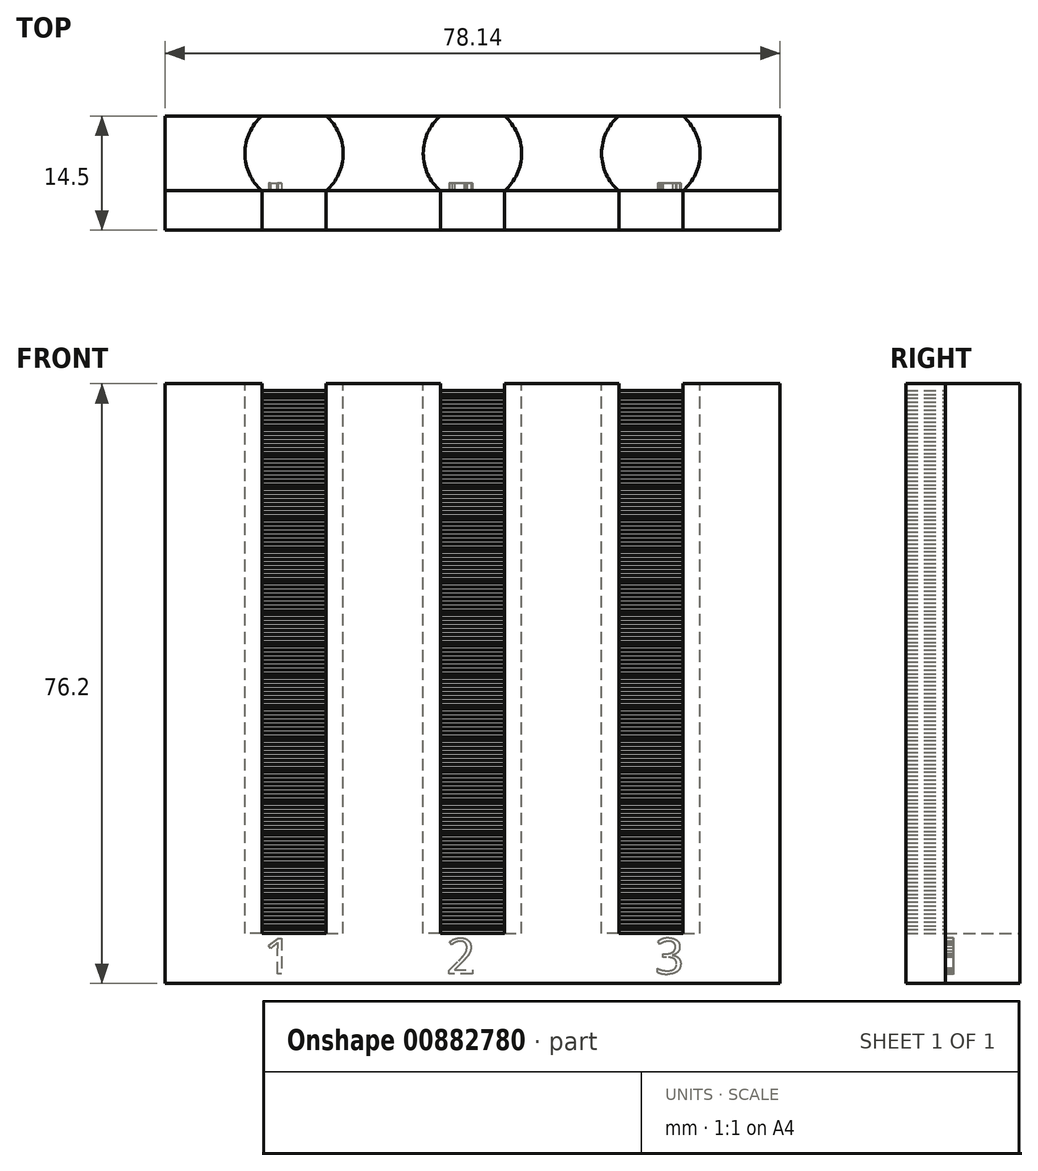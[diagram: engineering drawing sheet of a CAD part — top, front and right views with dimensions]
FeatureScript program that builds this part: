
annotation { "Feature Type Name" : "Feature", "Feature Type Description" : "" }
export const myFeature = defineFeature(function(context is Context, id is Id, definition is map)
    precondition{}
    {
        {
            var Q0;
            Q0=qCreatedBy(makeId("Top.planeOp"),FACE);
            var sketch = newSketch(context, id + "F0", { "sketchPlane" : qUnion([Q0])});
            skLineSegment(sketch, "E0.bottom", {"start": v(39.07, -4.75) * mm, "end": v(-39.07, -4.75) * mm});
            skLineSegment(sketch, "E0.top", {"start": v(39.07, 4.75) * mm, "end": v(-39.07, 4.75) * mm});
            skLineSegment(sketch, "E0.left", {"start": v(39.07, -4.75) * mm, "end": v(39.07, 4.75) * mm});
            skLineSegment(sketch, "E0.right", {"start": v(-39.07, -4.75) * mm, "end": v(-39.07, 4.75) * mm});
            skPoint(sketch, "E0.middle", {"position": v(0, 0) * mm});
            skSolve(sketch);
        }
        {
            var Q0;
            Q0 = qSketchRegion(id + "F0", true);
            extrude(context, id + "F1", {"entities" : qUnion([Q0]), "depth" : 76.2 * mm, "offsetDistance" : 25.4 * mm});
        }
        {
            var Q0;
            Q0=makeQuery(id+"F1.opExtrude","CAP_FACE",FACE,{"disambiguationData":[OSD([sQuery(id+"F0.wireOp",EDGE,"E0.bottom"),sQuery(id+"F0.wireOp",EDGE,"E0.top"),sQuery(id+"F0.wireOp",EDGE,"E0.left"),sQuery(id+"F0.wireOp",EDGE,"E0.right")])],"isStart":false});
            var sketch = newSketch(context, id + "F2", { "sketchPlane" : qUnion([Q0])});
            skCircle(sketch, "E1", {"center": v(-22.66, 0) * mm, "radius": 6.25 * mm});
            skCircle(sketch, "E2", {"center": v(0, 0) * mm, "radius": 6.25 * mm});
            skCircle(sketch, "E3", {"center": v(22.66, 0) * mm, "radius": 6.25 * mm});
            skLineSegment(sketch, "E4", {"start": v(0, -4.75) * mm, "end": v(0, 4.75) * mm});
            skSolve(sketch);
        }
        {
            var Q0;
            Q0 = qSketchRegion(id + "F2", true);
            extrude(context, id + "F3", {"entities" : qUnion([Q0]), "operationType" : NewBodyOperationType.REMOVE, "oppositeDirection" : true, "depth" : 69.85 * mm, "offsetDistance" : 25.4 * mm});
        }
        {
            var Q0;
            Q0=makeQuery(id+"F1.opExtrude","SWEPT_FACE",FACE,{"disambiguationData":[OSD([sQuery(id+"F0.wireOp",EDGE,"E0.bottom")])]});
            var sketch = newSketch(context, id + "F4", { "sketchPlane" : qUnion([Q0])});
            skText(sketch, "E5", { "text": "1            2              3", "fontName": "OpenSans-Regular.ttf"});
            const initialGuessF4  = {"E5": [-0.02647, 0.00124, 1, 0, 0.00453]};
            skSetInitialGuess(sketch, initialGuessF4);
            skSolve(sketch);
        }
        {
            var Q0;
            Q0 = qSketchRegion(id + "F4", true);
            extrude(context, id + "F5", {"entities" : qUnion([Q0]), "operationType" : NewBodyOperationType.REMOVE, "oppositeDirection" : true, "depth" : 1 * mm, "offsetDistance" : 25.4 * mm});
        }
        {
            var Q0;
            Q0=makeQuery(id+"F1.opExtrude","SWEPT_FACE",FACE,{"disambiguationData":[OSD([sQuery(id+"F0.wireOp",EDGE,"E0.bottom")])]});
            var sketch = newSketch(context, id + "F6", { "sketchPlane" : qUnion([Q0])});
            skLineSegment(sketch, "E6.bottom", {"start": v(-18.6, 6.85) * mm, "end": v(-26.72, 6.85) * mm});
            skLineSegment(sketch, "E6.top", {"start": v(-18.6, 7.35) * mm, "end": v(-26.72, 7.35) * mm});
            skLineSegment(sketch, "E6.left", {"start": v(-18.6, 6.85) * mm, "end": v(-18.6, 7.35) * mm});
            skLineSegment(sketch, "E6.right", {"start": v(-26.72, 6.85) * mm, "end": v(-26.72, 7.35) * mm});
            skLineSegment(sketch, "E7.0.1.0", {"start": v(-18.6, 8.35) * mm, "end": v(-26.72, 8.35) * mm});
            skLineSegment(sketch, "E7.0.1.1", {"start": v(-18.6, 7.85) * mm, "end": v(-26.72, 7.85) * mm});
            skLineSegment(sketch, "E7.0.1.2", {"start": v(-18.6, 7.85) * mm, "end": v(-18.6, 8.35) * mm});
            skLineSegment(sketch, "E7.0.1.3", {"start": v(-26.72, 7.85) * mm, "end": v(-26.72, 8.35) * mm});
            skLineSegment(sketch, "E7.0.2.0", {"start": v(-18.6, 9.35) * mm, "end": v(-26.72, 9.35) * mm});
            skLineSegment(sketch, "E7.0.2.1", {"start": v(-18.6, 8.85) * mm, "end": v(-26.72, 8.85) * mm});
            skLineSegment(sketch, "E7.0.2.2", {"start": v(-18.6, 8.85) * mm, "end": v(-18.6, 9.35) * mm});
            skLineSegment(sketch, "E7.0.2.3", {"start": v(-26.72, 8.85) * mm, "end": v(-26.72, 9.35) * mm});
            skLineSegment(sketch, "E7.0.3.0", {"start": v(-18.6, 10.35) * mm, "end": v(-26.72, 10.35) * mm});
            skLineSegment(sketch, "E7.0.3.1", {"start": v(-18.6, 9.85) * mm, "end": v(-26.72, 9.85) * mm});
            skLineSegment(sketch, "E7.0.3.2", {"start": v(-18.6, 9.85) * mm, "end": v(-18.6, 10.35) * mm});
            skLineSegment(sketch, "E7.0.3.3", {"start": v(-26.72, 9.85) * mm, "end": v(-26.72, 10.35) * mm});
            skLineSegment(sketch, "E7.0.4.0", {"start": v(-18.6, 11.35) * mm, "end": v(-26.72, 11.35) * mm});
            skLineSegment(sketch, "E7.0.4.1", {"start": v(-18.6, 10.85) * mm, "end": v(-26.72, 10.85) * mm});
            skLineSegment(sketch, "E7.0.4.2", {"start": v(-18.6, 10.85) * mm, "end": v(-18.6, 11.35) * mm});
            skLineSegment(sketch, "E7.0.4.3", {"start": v(-26.72, 10.85) * mm, "end": v(-26.72, 11.35) * mm});
            skLineSegment(sketch, "E7.0.5.0", {"start": v(-18.6, 12.35) * mm, "end": v(-26.72, 12.35) * mm});
            skLineSegment(sketch, "E7.0.5.1", {"start": v(-18.6, 11.85) * mm, "end": v(-26.72, 11.85) * mm});
            skLineSegment(sketch, "E7.0.5.2", {"start": v(-18.6, 11.85) * mm, "end": v(-18.6, 12.35) * mm});
            skLineSegment(sketch, "E7.0.5.3", {"start": v(-26.72, 11.85) * mm, "end": v(-26.72, 12.35) * mm});
            skLineSegment(sketch, "E7.0.6.0", {"start": v(-18.6, 13.35) * mm, "end": v(-26.72, 13.35) * mm});
            skLineSegment(sketch, "E7.0.6.1", {"start": v(-18.6, 12.85) * mm, "end": v(-26.72, 12.85) * mm});
            skLineSegment(sketch, "E7.0.6.2", {"start": v(-18.6, 12.85) * mm, "end": v(-18.6, 13.35) * mm});
            skLineSegment(sketch, "E7.0.6.3", {"start": v(-26.72, 12.85) * mm, "end": v(-26.72, 13.35) * mm});
            skLineSegment(sketch, "E7.0.7.0", {"start": v(-18.6, 14.35) * mm, "end": v(-26.72, 14.35) * mm});
            skLineSegment(sketch, "E7.0.7.1", {"start": v(-18.6, 13.85) * mm, "end": v(-26.72, 13.85) * mm});
            skLineSegment(sketch, "E7.0.7.2", {"start": v(-18.6, 13.85) * mm, "end": v(-18.6, 14.35) * mm});
            skLineSegment(sketch, "E7.0.7.3", {"start": v(-26.72, 13.85) * mm, "end": v(-26.72, 14.35) * mm});
            skLineSegment(sketch, "E7.0.8.0", {"start": v(-18.6, 15.35) * mm, "end": v(-26.72, 15.35) * mm});
            skLineSegment(sketch, "E7.0.8.1", {"start": v(-18.6, 14.85) * mm, "end": v(-26.72, 14.85) * mm});
            skLineSegment(sketch, "E7.0.8.2", {"start": v(-18.6, 14.85) * mm, "end": v(-18.6, 15.35) * mm});
            skLineSegment(sketch, "E7.0.8.3", {"start": v(-26.72, 14.85) * mm, "end": v(-26.72, 15.35) * mm});
            skLineSegment(sketch, "E7.0.9.0", {"start": v(-18.6, 16.35) * mm, "end": v(-26.72, 16.35) * mm});
            skLineSegment(sketch, "E7.0.9.1", {"start": v(-18.6, 15.85) * mm, "end": v(-26.72, 15.85) * mm});
            skLineSegment(sketch, "E7.0.9.2", {"start": v(-18.6, 15.85) * mm, "end": v(-18.6, 16.35) * mm});
            skLineSegment(sketch, "E7.0.9.3", {"start": v(-26.72, 15.85) * mm, "end": v(-26.72, 16.35) * mm});
            skLineSegment(sketch, "E7.0.10.0", {"start": v(-18.6, 17.35) * mm, "end": v(-26.72, 17.35) * mm});
            skLineSegment(sketch, "E7.0.10.1", {"start": v(-18.6, 16.85) * mm, "end": v(-26.72, 16.85) * mm});
            skLineSegment(sketch, "E7.0.10.2", {"start": v(-18.6, 16.85) * mm, "end": v(-18.6, 17.35) * mm});
            skLineSegment(sketch, "E7.0.10.3", {"start": v(-26.72, 16.85) * mm, "end": v(-26.72, 17.35) * mm});
            skLineSegment(sketch, "E7.0.11.0", {"start": v(-18.6, 18.35) * mm, "end": v(-26.72, 18.35) * mm});
            skLineSegment(sketch, "E7.0.11.1", {"start": v(-18.6, 17.85) * mm, "end": v(-26.72, 17.85) * mm});
            skLineSegment(sketch, "E7.0.11.2", {"start": v(-18.6, 17.85) * mm, "end": v(-18.6, 18.35) * mm});
            skLineSegment(sketch, "E7.0.11.3", {"start": v(-26.72, 17.85) * mm, "end": v(-26.72, 18.35) * mm});
            skLineSegment(sketch, "E7.0.12.0", {"start": v(-18.6, 19.35) * mm, "end": v(-26.72, 19.35) * mm});
            skLineSegment(sketch, "E7.0.12.1", {"start": v(-18.6, 18.85) * mm, "end": v(-26.72, 18.85) * mm});
            skLineSegment(sketch, "E7.0.12.2", {"start": v(-18.6, 18.85) * mm, "end": v(-18.6, 19.35) * mm});
            skLineSegment(sketch, "E7.0.12.3", {"start": v(-26.72, 18.85) * mm, "end": v(-26.72, 19.35) * mm});
            skLineSegment(sketch, "E7.0.13.0", {"start": v(-18.6, 20.35) * mm, "end": v(-26.72, 20.35) * mm});
            skLineSegment(sketch, "E7.0.13.1", {"start": v(-18.6, 19.85) * mm, "end": v(-26.72, 19.85) * mm});
            skLineSegment(sketch, "E7.0.13.2", {"start": v(-18.6, 19.85) * mm, "end": v(-18.6, 20.35) * mm});
            skLineSegment(sketch, "E7.0.13.3", {"start": v(-26.72, 19.85) * mm, "end": v(-26.72, 20.35) * mm});
            skLineSegment(sketch, "E7.0.14.0", {"start": v(-18.6, 21.35) * mm, "end": v(-26.72, 21.35) * mm});
            skLineSegment(sketch, "E7.0.14.1", {"start": v(-18.6, 20.85) * mm, "end": v(-26.72, 20.85) * mm});
            skLineSegment(sketch, "E7.0.14.2", {"start": v(-18.6, 20.85) * mm, "end": v(-18.6, 21.35) * mm});
            skLineSegment(sketch, "E7.0.14.3", {"start": v(-26.72, 20.85) * mm, "end": v(-26.72, 21.35) * mm});
            skLineSegment(sketch, "E7.0.15.0", {"start": v(-18.6, 22.35) * mm, "end": v(-26.72, 22.35) * mm});
            skLineSegment(sketch, "E7.0.15.1", {"start": v(-18.6, 21.85) * mm, "end": v(-26.72, 21.85) * mm});
            skLineSegment(sketch, "E7.0.15.2", {"start": v(-18.6, 21.85) * mm, "end": v(-18.6, 22.35) * mm});
            skLineSegment(sketch, "E7.0.15.3", {"start": v(-26.72, 21.85) * mm, "end": v(-26.72, 22.35) * mm});
            skLineSegment(sketch, "E7.0.16.0", {"start": v(-18.6, 23.35) * mm, "end": v(-26.72, 23.35) * mm});
            skLineSegment(sketch, "E7.0.16.1", {"start": v(-18.6, 22.85) * mm, "end": v(-26.72, 22.85) * mm});
            skLineSegment(sketch, "E7.0.16.2", {"start": v(-18.6, 22.85) * mm, "end": v(-18.6, 23.35) * mm});
            skLineSegment(sketch, "E7.0.16.3", {"start": v(-26.72, 22.85) * mm, "end": v(-26.72, 23.35) * mm});
            skLineSegment(sketch, "E7.0.17.0", {"start": v(-18.6, 24.35) * mm, "end": v(-26.72, 24.35) * mm});
            skLineSegment(sketch, "E7.0.17.1", {"start": v(-18.6, 23.85) * mm, "end": v(-26.72, 23.85) * mm});
            skLineSegment(sketch, "E7.0.17.2", {"start": v(-18.6, 23.85) * mm, "end": v(-18.6, 24.35) * mm});
            skLineSegment(sketch, "E7.0.17.3", {"start": v(-26.72, 23.85) * mm, "end": v(-26.72, 24.35) * mm});
            skLineSegment(sketch, "E7.0.18.0", {"start": v(-18.6, 25.35) * mm, "end": v(-26.72, 25.35) * mm});
            skLineSegment(sketch, "E7.0.18.1", {"start": v(-18.6, 24.85) * mm, "end": v(-26.72, 24.85) * mm});
            skLineSegment(sketch, "E7.0.18.2", {"start": v(-18.6, 24.85) * mm, "end": v(-18.6, 25.35) * mm});
            skLineSegment(sketch, "E7.0.18.3", {"start": v(-26.72, 24.85) * mm, "end": v(-26.72, 25.35) * mm});
            skLineSegment(sketch, "E7.0.19.0", {"start": v(-18.6, 26.35) * mm, "end": v(-26.72, 26.35) * mm});
            skLineSegment(sketch, "E7.0.19.1", {"start": v(-18.6, 25.85) * mm, "end": v(-26.72, 25.85) * mm});
            skLineSegment(sketch, "E7.0.19.2", {"start": v(-18.6, 25.85) * mm, "end": v(-18.6, 26.35) * mm});
            skLineSegment(sketch, "E7.0.19.3", {"start": v(-26.72, 25.85) * mm, "end": v(-26.72, 26.35) * mm});
            skLineSegment(sketch, "E7.0.20.0", {"start": v(-18.6, 27.35) * mm, "end": v(-26.72, 27.35) * mm});
            skLineSegment(sketch, "E7.0.20.1", {"start": v(-18.6, 26.85) * mm, "end": v(-26.72, 26.85) * mm});
            skLineSegment(sketch, "E7.0.20.2", {"start": v(-18.6, 26.85) * mm, "end": v(-18.6, 27.35) * mm});
            skLineSegment(sketch, "E7.0.20.3", {"start": v(-26.72, 26.85) * mm, "end": v(-26.72, 27.35) * mm});
            skLineSegment(sketch, "E7.0.21.0", {"start": v(-18.6, 28.35) * mm, "end": v(-26.72, 28.35) * mm});
            skLineSegment(sketch, "E7.0.21.1", {"start": v(-18.6, 27.85) * mm, "end": v(-26.72, 27.85) * mm});
            skLineSegment(sketch, "E7.0.21.2", {"start": v(-18.6, 27.85) * mm, "end": v(-18.6, 28.35) * mm});
            skLineSegment(sketch, "E7.0.21.3", {"start": v(-26.72, 27.85) * mm, "end": v(-26.72, 28.35) * mm});
            skLineSegment(sketch, "E7.0.22.0", {"start": v(-18.6, 29.35) * mm, "end": v(-26.72, 29.35) * mm});
            skLineSegment(sketch, "E7.0.22.1", {"start": v(-18.6, 28.85) * mm, "end": v(-26.72, 28.85) * mm});
            skLineSegment(sketch, "E7.0.22.2", {"start": v(-18.6, 28.85) * mm, "end": v(-18.6, 29.35) * mm});
            skLineSegment(sketch, "E7.0.22.3", {"start": v(-26.72, 28.85) * mm, "end": v(-26.72, 29.35) * mm});
            skLineSegment(sketch, "E7.0.23.0", {"start": v(-18.6, 30.35) * mm, "end": v(-26.72, 30.35) * mm});
            skLineSegment(sketch, "E7.0.23.1", {"start": v(-18.6, 29.85) * mm, "end": v(-26.72, 29.85) * mm});
            skLineSegment(sketch, "E7.0.23.2", {"start": v(-18.6, 29.85) * mm, "end": v(-18.6, 30.35) * mm});
            skLineSegment(sketch, "E7.0.23.3", {"start": v(-26.72, 29.85) * mm, "end": v(-26.72, 30.35) * mm});
            skLineSegment(sketch, "E7.0.24.0", {"start": v(-18.6, 31.35) * mm, "end": v(-26.72, 31.35) * mm});
            skLineSegment(sketch, "E7.0.24.1", {"start": v(-18.6, 30.85) * mm, "end": v(-26.72, 30.85) * mm});
            skLineSegment(sketch, "E7.0.24.2", {"start": v(-18.6, 30.85) * mm, "end": v(-18.6, 31.35) * mm});
            skLineSegment(sketch, "E7.0.24.3", {"start": v(-26.72, 30.85) * mm, "end": v(-26.72, 31.35) * mm});
            skLineSegment(sketch, "E7.0.25.0", {"start": v(-18.6, 32.35) * mm, "end": v(-26.72, 32.35) * mm});
            skLineSegment(sketch, "E7.0.25.1", {"start": v(-18.6, 31.85) * mm, "end": v(-26.72, 31.85) * mm});
            skLineSegment(sketch, "E7.0.25.2", {"start": v(-18.6, 31.85) * mm, "end": v(-18.6, 32.35) * mm});
            skLineSegment(sketch, "E7.0.25.3", {"start": v(-26.72, 31.85) * mm, "end": v(-26.72, 32.35) * mm});
            skLineSegment(sketch, "E7.0.26.0", {"start": v(-18.6, 33.35) * mm, "end": v(-26.72, 33.35) * mm});
            skLineSegment(sketch, "E7.0.26.1", {"start": v(-18.6, 32.85) * mm, "end": v(-26.72, 32.85) * mm});
            skLineSegment(sketch, "E7.0.26.2", {"start": v(-18.6, 32.85) * mm, "end": v(-18.6, 33.35) * mm});
            skLineSegment(sketch, "E7.0.26.3", {"start": v(-26.72, 32.85) * mm, "end": v(-26.72, 33.35) * mm});
            skLineSegment(sketch, "E7.0.27.0", {"start": v(-18.6, 34.35) * mm, "end": v(-26.72, 34.35) * mm});
            skLineSegment(sketch, "E7.0.27.1", {"start": v(-18.6, 33.85) * mm, "end": v(-26.72, 33.85) * mm});
            skLineSegment(sketch, "E7.0.27.2", {"start": v(-18.6, 33.85) * mm, "end": v(-18.6, 34.35) * mm});
            skLineSegment(sketch, "E7.0.27.3", {"start": v(-26.72, 33.85) * mm, "end": v(-26.72, 34.35) * mm});
            skLineSegment(sketch, "E7.0.28.0", {"start": v(-18.6, 35.35) * mm, "end": v(-26.72, 35.35) * mm});
            skLineSegment(sketch, "E7.0.28.1", {"start": v(-18.6, 34.85) * mm, "end": v(-26.72, 34.85) * mm});
            skLineSegment(sketch, "E7.0.28.2", {"start": v(-18.6, 34.85) * mm, "end": v(-18.6, 35.35) * mm});
            skLineSegment(sketch, "E7.0.28.3", {"start": v(-26.72, 34.85) * mm, "end": v(-26.72, 35.35) * mm});
            skLineSegment(sketch, "E7.0.29.0", {"start": v(-18.6, 36.35) * mm, "end": v(-26.72, 36.35) * mm});
            skLineSegment(sketch, "E7.0.29.1", {"start": v(-18.6, 35.85) * mm, "end": v(-26.72, 35.85) * mm});
            skLineSegment(sketch, "E7.0.29.2", {"start": v(-18.6, 35.85) * mm, "end": v(-18.6, 36.35) * mm});
            skLineSegment(sketch, "E7.0.29.3", {"start": v(-26.72, 35.85) * mm, "end": v(-26.72, 36.35) * mm});
            skLineSegment(sketch, "E7.0.30.0", {"start": v(-18.6, 37.35) * mm, "end": v(-26.72, 37.35) * mm});
            skLineSegment(sketch, "E7.0.30.1", {"start": v(-18.6, 36.85) * mm, "end": v(-26.72, 36.85) * mm});
            skLineSegment(sketch, "E7.0.30.2", {"start": v(-18.6, 36.85) * mm, "end": v(-18.6, 37.35) * mm});
            skLineSegment(sketch, "E7.0.30.3", {"start": v(-26.72, 36.85) * mm, "end": v(-26.72, 37.35) * mm});
            skLineSegment(sketch, "E7.0.31.0", {"start": v(-18.6, 38.35) * mm, "end": v(-26.72, 38.35) * mm});
            skLineSegment(sketch, "E7.0.31.1", {"start": v(-18.6, 37.85) * mm, "end": v(-26.72, 37.85) * mm});
            skLineSegment(sketch, "E7.0.31.2", {"start": v(-18.6, 37.85) * mm, "end": v(-18.6, 38.35) * mm});
            skLineSegment(sketch, "E7.0.31.3", {"start": v(-26.72, 37.85) * mm, "end": v(-26.72, 38.35) * mm});
            skLineSegment(sketch, "E7.0.32.0", {"start": v(-18.6, 39.35) * mm, "end": v(-26.72, 39.35) * mm});
            skLineSegment(sketch, "E7.0.32.1", {"start": v(-18.6, 38.85) * mm, "end": v(-26.72, 38.85) * mm});
            skLineSegment(sketch, "E7.0.32.2", {"start": v(-18.6, 38.85) * mm, "end": v(-18.6, 39.35) * mm});
            skLineSegment(sketch, "E7.0.32.3", {"start": v(-26.72, 38.85) * mm, "end": v(-26.72, 39.35) * mm});
            skLineSegment(sketch, "E7.0.33.0", {"start": v(-18.6, 40.35) * mm, "end": v(-26.72, 40.35) * mm});
            skLineSegment(sketch, "E7.0.33.1", {"start": v(-18.6, 39.85) * mm, "end": v(-26.72, 39.85) * mm});
            skLineSegment(sketch, "E7.0.33.2", {"start": v(-18.6, 39.85) * mm, "end": v(-18.6, 40.35) * mm});
            skLineSegment(sketch, "E7.0.33.3", {"start": v(-26.72, 39.85) * mm, "end": v(-26.72, 40.35) * mm});
            skLineSegment(sketch, "E7.0.34.0", {"start": v(-18.6, 41.35) * mm, "end": v(-26.72, 41.35) * mm});
            skLineSegment(sketch, "E7.0.34.1", {"start": v(-18.6, 40.85) * mm, "end": v(-26.72, 40.85) * mm});
            skLineSegment(sketch, "E7.0.34.2", {"start": v(-18.6, 40.85) * mm, "end": v(-18.6, 41.35) * mm});
            skLineSegment(sketch, "E7.0.34.3", {"start": v(-26.72, 40.85) * mm, "end": v(-26.72, 41.35) * mm});
            skLineSegment(sketch, "E7.0.35.0", {"start": v(-18.6, 42.35) * mm, "end": v(-26.72, 42.35) * mm});
            skLineSegment(sketch, "E7.0.35.1", {"start": v(-18.6, 41.85) * mm, "end": v(-26.72, 41.85) * mm});
            skLineSegment(sketch, "E7.0.35.2", {"start": v(-18.6, 41.85) * mm, "end": v(-18.6, 42.35) * mm});
            skLineSegment(sketch, "E7.0.35.3", {"start": v(-26.72, 41.85) * mm, "end": v(-26.72, 42.35) * mm});
            skLineSegment(sketch, "E7.0.36.0", {"start": v(-18.6, 43.35) * mm, "end": v(-26.72, 43.35) * mm});
            skLineSegment(sketch, "E7.0.36.1", {"start": v(-18.6, 42.85) * mm, "end": v(-26.72, 42.85) * mm});
            skLineSegment(sketch, "E7.0.36.2", {"start": v(-18.6, 42.85) * mm, "end": v(-18.6, 43.35) * mm});
            skLineSegment(sketch, "E7.0.36.3", {"start": v(-26.72, 42.85) * mm, "end": v(-26.72, 43.35) * mm});
            skLineSegment(sketch, "E7.0.37.0", {"start": v(-18.6, 44.35) * mm, "end": v(-26.72, 44.35) * mm});
            skLineSegment(sketch, "E7.0.37.1", {"start": v(-18.6, 43.85) * mm, "end": v(-26.72, 43.85) * mm});
            skLineSegment(sketch, "E7.0.37.2", {"start": v(-18.6, 43.85) * mm, "end": v(-18.6, 44.35) * mm});
            skLineSegment(sketch, "E7.0.37.3", {"start": v(-26.72, 43.85) * mm, "end": v(-26.72, 44.35) * mm});
            skLineSegment(sketch, "E7.0.38.0", {"start": v(-18.6, 45.35) * mm, "end": v(-26.72, 45.35) * mm});
            skLineSegment(sketch, "E7.0.38.1", {"start": v(-18.6, 44.85) * mm, "end": v(-26.72, 44.85) * mm});
            skLineSegment(sketch, "E7.0.38.2", {"start": v(-18.6, 44.85) * mm, "end": v(-18.6, 45.35) * mm});
            skLineSegment(sketch, "E7.0.38.3", {"start": v(-26.72, 44.85) * mm, "end": v(-26.72, 45.35) * mm});
            skLineSegment(sketch, "E7.0.39.0", {"start": v(-18.6, 46.35) * mm, "end": v(-26.72, 46.35) * mm});
            skLineSegment(sketch, "E7.0.39.1", {"start": v(-18.6, 45.85) * mm, "end": v(-26.72, 45.85) * mm});
            skLineSegment(sketch, "E7.0.39.2", {"start": v(-18.6, 45.85) * mm, "end": v(-18.6, 46.35) * mm});
            skLineSegment(sketch, "E7.0.39.3", {"start": v(-26.72, 45.85) * mm, "end": v(-26.72, 46.35) * mm});
            skLineSegment(sketch, "E7.0.40.0", {"start": v(-18.6, 47.35) * mm, "end": v(-26.72, 47.35) * mm});
            skLineSegment(sketch, "E7.0.40.1", {"start": v(-18.6, 46.85) * mm, "end": v(-26.72, 46.85) * mm});
            skLineSegment(sketch, "E7.0.40.2", {"start": v(-18.6, 46.85) * mm, "end": v(-18.6, 47.35) * mm});
            skLineSegment(sketch, "E7.0.40.3", {"start": v(-26.72, 46.85) * mm, "end": v(-26.72, 47.35) * mm});
            skLineSegment(sketch, "E7.0.41.0", {"start": v(-18.6, 48.35) * mm, "end": v(-26.72, 48.35) * mm});
            skLineSegment(sketch, "E7.0.41.1", {"start": v(-18.6, 47.85) * mm, "end": v(-26.72, 47.85) * mm});
            skLineSegment(sketch, "E7.0.41.2", {"start": v(-18.6, 47.85) * mm, "end": v(-18.6, 48.35) * mm});
            skLineSegment(sketch, "E7.0.41.3", {"start": v(-26.72, 47.85) * mm, "end": v(-26.72, 48.35) * mm});
            skLineSegment(sketch, "E7.0.42.0", {"start": v(-18.6, 49.35) * mm, "end": v(-26.72, 49.35) * mm});
            skLineSegment(sketch, "E7.0.42.1", {"start": v(-18.6, 48.85) * mm, "end": v(-26.72, 48.85) * mm});
            skLineSegment(sketch, "E7.0.42.2", {"start": v(-18.6, 48.85) * mm, "end": v(-18.6, 49.35) * mm});
            skLineSegment(sketch, "E7.0.42.3", {"start": v(-26.72, 48.85) * mm, "end": v(-26.72, 49.35) * mm});
            skLineSegment(sketch, "E7.0.43.0", {"start": v(-18.6, 50.35) * mm, "end": v(-26.72, 50.35) * mm});
            skLineSegment(sketch, "E7.0.43.1", {"start": v(-18.6, 49.85) * mm, "end": v(-26.72, 49.85) * mm});
            skLineSegment(sketch, "E7.0.43.2", {"start": v(-18.6, 49.85) * mm, "end": v(-18.6, 50.35) * mm});
            skLineSegment(sketch, "E7.0.43.3", {"start": v(-26.72, 49.85) * mm, "end": v(-26.72, 50.35) * mm});
            skLineSegment(sketch, "E7.0.44.0", {"start": v(-18.6, 51.35) * mm, "end": v(-26.72, 51.35) * mm});
            skLineSegment(sketch, "E7.0.44.1", {"start": v(-18.6, 50.85) * mm, "end": v(-26.72, 50.85) * mm});
            skLineSegment(sketch, "E7.0.44.2", {"start": v(-18.6, 50.85) * mm, "end": v(-18.6, 51.35) * mm});
            skLineSegment(sketch, "E7.0.44.3", {"start": v(-26.72, 50.85) * mm, "end": v(-26.72, 51.35) * mm});
            skLineSegment(sketch, "E7.0.45.0", {"start": v(-18.6, 52.35) * mm, "end": v(-26.72, 52.35) * mm});
            skLineSegment(sketch, "E7.0.45.1", {"start": v(-18.6, 51.85) * mm, "end": v(-26.72, 51.85) * mm});
            skLineSegment(sketch, "E7.0.45.2", {"start": v(-18.6, 51.85) * mm, "end": v(-18.6, 52.35) * mm});
            skLineSegment(sketch, "E7.0.45.3", {"start": v(-26.72, 51.85) * mm, "end": v(-26.72, 52.35) * mm});
            skLineSegment(sketch, "E7.0.46.0", {"start": v(-18.6, 53.35) * mm, "end": v(-26.72, 53.35) * mm});
            skLineSegment(sketch, "E7.0.46.1", {"start": v(-18.6, 52.85) * mm, "end": v(-26.72, 52.85) * mm});
            skLineSegment(sketch, "E7.0.46.2", {"start": v(-18.6, 52.85) * mm, "end": v(-18.6, 53.35) * mm});
            skLineSegment(sketch, "E7.0.46.3", {"start": v(-26.72, 52.85) * mm, "end": v(-26.72, 53.35) * mm});
            skLineSegment(sketch, "E7.0.47.0", {"start": v(-18.6, 54.35) * mm, "end": v(-26.72, 54.35) * mm});
            skLineSegment(sketch, "E7.0.47.1", {"start": v(-18.6, 53.85) * mm, "end": v(-26.72, 53.85) * mm});
            skLineSegment(sketch, "E7.0.47.2", {"start": v(-18.6, 53.85) * mm, "end": v(-18.6, 54.35) * mm});
            skLineSegment(sketch, "E7.0.47.3", {"start": v(-26.72, 53.85) * mm, "end": v(-26.72, 54.35) * mm});
            skLineSegment(sketch, "E7.0.48.0", {"start": v(-18.6, 55.35) * mm, "end": v(-26.72, 55.35) * mm});
            skLineSegment(sketch, "E7.0.48.1", {"start": v(-18.6, 54.85) * mm, "end": v(-26.72, 54.85) * mm});
            skLineSegment(sketch, "E7.0.48.2", {"start": v(-18.6, 54.85) * mm, "end": v(-18.6, 55.35) * mm});
            skLineSegment(sketch, "E7.0.48.3", {"start": v(-26.72, 54.85) * mm, "end": v(-26.72, 55.35) * mm});
            skLineSegment(sketch, "E7.0.49.0", {"start": v(-18.6, 56.35) * mm, "end": v(-26.72, 56.35) * mm});
            skLineSegment(sketch, "E7.0.49.1", {"start": v(-18.6, 55.85) * mm, "end": v(-26.72, 55.85) * mm});
            skLineSegment(sketch, "E7.0.49.2", {"start": v(-18.6, 55.85) * mm, "end": v(-18.6, 56.35) * mm});
            skLineSegment(sketch, "E7.0.49.3", {"start": v(-26.72, 55.85) * mm, "end": v(-26.72, 56.35) * mm});
            skLineSegment(sketch, "E7.0.50.0", {"start": v(-18.6, 57.35) * mm, "end": v(-26.72, 57.35) * mm});
            skLineSegment(sketch, "E7.0.50.1", {"start": v(-18.6, 56.85) * mm, "end": v(-26.72, 56.85) * mm});
            skLineSegment(sketch, "E7.0.50.2", {"start": v(-18.6, 56.85) * mm, "end": v(-18.6, 57.35) * mm});
            skLineSegment(sketch, "E7.0.50.3", {"start": v(-26.72, 56.85) * mm, "end": v(-26.72, 57.35) * mm});
            skLineSegment(sketch, "E7.0.51.0", {"start": v(-18.6, 58.35) * mm, "end": v(-26.72, 58.35) * mm});
            skLineSegment(sketch, "E7.0.51.1", {"start": v(-18.6, 57.85) * mm, "end": v(-26.72, 57.85) * mm});
            skLineSegment(sketch, "E7.0.51.2", {"start": v(-18.6, 57.85) * mm, "end": v(-18.6, 58.35) * mm});
            skLineSegment(sketch, "E7.0.51.3", {"start": v(-26.72, 57.85) * mm, "end": v(-26.72, 58.35) * mm});
            skLineSegment(sketch, "E7.0.52.0", {"start": v(-18.6, 59.35) * mm, "end": v(-26.72, 59.35) * mm});
            skLineSegment(sketch, "E7.0.52.1", {"start": v(-18.6, 58.85) * mm, "end": v(-26.72, 58.85) * mm});
            skLineSegment(sketch, "E7.0.52.2", {"start": v(-18.6, 58.85) * mm, "end": v(-18.6, 59.35) * mm});
            skLineSegment(sketch, "E7.0.52.3", {"start": v(-26.72, 58.85) * mm, "end": v(-26.72, 59.35) * mm});
            skLineSegment(sketch, "E7.0.53.0", {"start": v(-18.6, 60.35) * mm, "end": v(-26.72, 60.35) * mm});
            skLineSegment(sketch, "E7.0.53.1", {"start": v(-18.6, 59.85) * mm, "end": v(-26.72, 59.85) * mm});
            skLineSegment(sketch, "E7.0.53.2", {"start": v(-18.6, 59.85) * mm, "end": v(-18.6, 60.35) * mm});
            skLineSegment(sketch, "E7.0.53.3", {"start": v(-26.72, 59.85) * mm, "end": v(-26.72, 60.35) * mm});
            skLineSegment(sketch, "E7.0.54.0", {"start": v(-18.6, 61.35) * mm, "end": v(-26.72, 61.35) * mm});
            skLineSegment(sketch, "E7.0.54.1", {"start": v(-18.6, 60.85) * mm, "end": v(-26.72, 60.85) * mm});
            skLineSegment(sketch, "E7.0.54.2", {"start": v(-18.6, 60.85) * mm, "end": v(-18.6, 61.35) * mm});
            skLineSegment(sketch, "E7.0.54.3", {"start": v(-26.72, 60.85) * mm, "end": v(-26.72, 61.35) * mm});
            skLineSegment(sketch, "E7.0.55.0", {"start": v(-18.6, 62.35) * mm, "end": v(-26.72, 62.35) * mm});
            skLineSegment(sketch, "E7.0.55.1", {"start": v(-18.6, 61.85) * mm, "end": v(-26.72, 61.85) * mm});
            skLineSegment(sketch, "E7.0.55.2", {"start": v(-18.6, 61.85) * mm, "end": v(-18.6, 62.35) * mm});
            skLineSegment(sketch, "E7.0.55.3", {"start": v(-26.72, 61.85) * mm, "end": v(-26.72, 62.35) * mm});
            skLineSegment(sketch, "E7.0.56.0", {"start": v(-18.6, 63.35) * mm, "end": v(-26.72, 63.35) * mm});
            skLineSegment(sketch, "E7.0.56.1", {"start": v(-18.6, 62.85) * mm, "end": v(-26.72, 62.85) * mm});
            skLineSegment(sketch, "E7.0.56.2", {"start": v(-18.6, 62.85) * mm, "end": v(-18.6, 63.35) * mm});
            skLineSegment(sketch, "E7.0.56.3", {"start": v(-26.72, 62.85) * mm, "end": v(-26.72, 63.35) * mm});
            skLineSegment(sketch, "E7.0.57.0", {"start": v(-18.6, 64.35) * mm, "end": v(-26.72, 64.35) * mm});
            skLineSegment(sketch, "E7.0.57.1", {"start": v(-18.6, 63.85) * mm, "end": v(-26.72, 63.85) * mm});
            skLineSegment(sketch, "E7.0.57.2", {"start": v(-18.6, 63.85) * mm, "end": v(-18.6, 64.35) * mm});
            skLineSegment(sketch, "E7.0.57.3", {"start": v(-26.72, 63.85) * mm, "end": v(-26.72, 64.35) * mm});
            skLineSegment(sketch, "E7.0.58.0", {"start": v(-18.6, 65.35) * mm, "end": v(-26.72, 65.35) * mm});
            skLineSegment(sketch, "E7.0.58.1", {"start": v(-18.6, 64.85) * mm, "end": v(-26.72, 64.85) * mm});
            skLineSegment(sketch, "E7.0.58.2", {"start": v(-18.6, 64.85) * mm, "end": v(-18.6, 65.35) * mm});
            skLineSegment(sketch, "E7.0.58.3", {"start": v(-26.72, 64.85) * mm, "end": v(-26.72, 65.35) * mm});
            skLineSegment(sketch, "E7.0.59.0", {"start": v(-18.6, 66.35) * mm, "end": v(-26.72, 66.35) * mm});
            skLineSegment(sketch, "E7.0.59.1", {"start": v(-18.6, 65.85) * mm, "end": v(-26.72, 65.85) * mm});
            skLineSegment(sketch, "E7.0.59.2", {"start": v(-18.6, 65.85) * mm, "end": v(-18.6, 66.35) * mm});
            skLineSegment(sketch, "E7.0.59.3", {"start": v(-26.72, 65.85) * mm, "end": v(-26.72, 66.35) * mm});
            skLineSegment(sketch, "E7.0.60.0", {"start": v(-18.6, 67.35) * mm, "end": v(-26.72, 67.35) * mm});
            skLineSegment(sketch, "E7.0.60.1", {"start": v(-18.6, 66.85) * mm, "end": v(-26.72, 66.85) * mm});
            skLineSegment(sketch, "E7.0.60.2", {"start": v(-18.6, 66.85) * mm, "end": v(-18.6, 67.35) * mm});
            skLineSegment(sketch, "E7.0.60.3", {"start": v(-26.72, 66.85) * mm, "end": v(-26.72, 67.35) * mm});
            skLineSegment(sketch, "E7.0.61.0", {"start": v(-18.6, 68.35) * mm, "end": v(-26.72, 68.35) * mm});
            skLineSegment(sketch, "E7.0.61.1", {"start": v(-18.6, 67.85) * mm, "end": v(-26.72, 67.85) * mm});
            skLineSegment(sketch, "E7.0.61.2", {"start": v(-18.6, 67.85) * mm, "end": v(-18.6, 68.35) * mm});
            skLineSegment(sketch, "E7.0.61.3", {"start": v(-26.72, 67.85) * mm, "end": v(-26.72, 68.35) * mm});
            skLineSegment(sketch, "E7.0.62.0", {"start": v(-18.6, 69.35) * mm, "end": v(-26.72, 69.35) * mm});
            skLineSegment(sketch, "E7.0.62.1", {"start": v(-18.6, 68.85) * mm, "end": v(-26.72, 68.85) * mm});
            skLineSegment(sketch, "E7.0.62.2", {"start": v(-18.6, 68.85) * mm, "end": v(-18.6, 69.35) * mm});
            skLineSegment(sketch, "E7.0.62.3", {"start": v(-26.72, 68.85) * mm, "end": v(-26.72, 69.35) * mm});
            skLineSegment(sketch, "E7.0.63.0", {"start": v(-18.6, 70.35) * mm, "end": v(-26.72, 70.35) * mm});
            skLineSegment(sketch, "E7.0.63.1", {"start": v(-18.6, 69.85) * mm, "end": v(-26.72, 69.85) * mm});
            skLineSegment(sketch, "E7.0.63.2", {"start": v(-18.6, 69.85) * mm, "end": v(-18.6, 70.35) * mm});
            skLineSegment(sketch, "E7.0.63.3", {"start": v(-26.72, 69.85) * mm, "end": v(-26.72, 70.35) * mm});
            skLineSegment(sketch, "E7.0.64.0", {"start": v(-18.6, 71.35) * mm, "end": v(-26.72, 71.35) * mm});
            skLineSegment(sketch, "E7.0.64.1", {"start": v(-18.6, 70.85) * mm, "end": v(-26.72, 70.85) * mm});
            skLineSegment(sketch, "E7.0.64.2", {"start": v(-18.6, 70.85) * mm, "end": v(-18.6, 71.35) * mm});
            skLineSegment(sketch, "E7.0.64.3", {"start": v(-26.72, 70.85) * mm, "end": v(-26.72, 71.35) * mm});
            skLineSegment(sketch, "E7.0.65.0", {"start": v(-18.6, 72.35) * mm, "end": v(-26.72, 72.35) * mm});
            skLineSegment(sketch, "E7.0.65.1", {"start": v(-18.6, 71.85) * mm, "end": v(-26.72, 71.85) * mm});
            skLineSegment(sketch, "E7.0.65.2", {"start": v(-18.6, 71.85) * mm, "end": v(-18.6, 72.35) * mm});
            skLineSegment(sketch, "E7.0.65.3", {"start": v(-26.72, 71.85) * mm, "end": v(-26.72, 72.35) * mm});
            skLineSegment(sketch, "E7.0.66.0", {"start": v(-18.6, 73.35) * mm, "end": v(-26.72, 73.35) * mm});
            skLineSegment(sketch, "E7.0.66.1", {"start": v(-18.6, 72.85) * mm, "end": v(-26.72, 72.85) * mm});
            skLineSegment(sketch, "E7.0.66.2", {"start": v(-18.6, 72.85) * mm, "end": v(-18.6, 73.35) * mm});
            skLineSegment(sketch, "E7.0.66.3", {"start": v(-26.72, 72.85) * mm, "end": v(-26.72, 73.35) * mm});
            skLineSegment(sketch, "E7.0.67.0", {"start": v(-18.6, 74.35) * mm, "end": v(-26.72, 74.35) * mm});
            skLineSegment(sketch, "E7.0.67.1", {"start": v(-18.6, 73.85) * mm, "end": v(-26.72, 73.85) * mm});
            skLineSegment(sketch, "E7.0.67.2", {"start": v(-18.6, 73.85) * mm, "end": v(-18.6, 74.35) * mm});
            skLineSegment(sketch, "E7.0.67.3", {"start": v(-26.72, 73.85) * mm, "end": v(-26.72, 74.35) * mm});
            skLineSegment(sketch, "E7.0.68.0", {"start": v(-18.6, 75.35) * mm, "end": v(-26.72, 75.35) * mm});
            skLineSegment(sketch, "E7.0.68.1", {"start": v(-18.6, 74.85) * mm, "end": v(-26.72, 74.85) * mm});
            skLineSegment(sketch, "E7.0.68.2", {"start": v(-18.6, 74.85) * mm, "end": v(-18.6, 75.35) * mm});
            skLineSegment(sketch, "E7.0.68.3", {"start": v(-26.72, 74.85) * mm, "end": v(-26.72, 75.35) * mm});
            skLineSegment(sketch, "E7.1.0.0", {"start": v(4.06, 7.35) * mm, "end": v(-4.06, 7.35) * mm});
            skLineSegment(sketch, "E7.1.0.1", {"start": v(4.06, 6.85) * mm, "end": v(-4.06, 6.85) * mm});
            skLineSegment(sketch, "E7.1.0.2", {"start": v(4.06, 6.85) * mm, "end": v(4.06, 7.35) * mm});
            skLineSegment(sketch, "E7.1.0.3", {"start": v(-4.06, 6.85) * mm, "end": v(-4.06, 7.35) * mm});
            skLineSegment(sketch, "E7.1.1.0", {"start": v(4.06, 8.35) * mm, "end": v(-4.06, 8.35) * mm});
            skLineSegment(sketch, "E7.1.1.1", {"start": v(4.06, 7.85) * mm, "end": v(-4.06, 7.85) * mm});
            skLineSegment(sketch, "E7.1.1.2", {"start": v(4.06, 7.85) * mm, "end": v(4.06, 8.35) * mm});
            skLineSegment(sketch, "E7.1.1.3", {"start": v(-4.06, 7.85) * mm, "end": v(-4.06, 8.35) * mm});
            skLineSegment(sketch, "E7.1.2.0", {"start": v(4.06, 9.35) * mm, "end": v(-4.06, 9.35) * mm});
            skLineSegment(sketch, "E7.1.2.1", {"start": v(4.06, 8.85) * mm, "end": v(-4.06, 8.85) * mm});
            skLineSegment(sketch, "E7.1.2.2", {"start": v(4.06, 8.85) * mm, "end": v(4.06, 9.35) * mm});
            skLineSegment(sketch, "E7.1.2.3", {"start": v(-4.06, 8.85) * mm, "end": v(-4.06, 9.35) * mm});
            skLineSegment(sketch, "E7.1.3.0", {"start": v(4.06, 10.35) * mm, "end": v(-4.06, 10.35) * mm});
            skLineSegment(sketch, "E7.1.3.1", {"start": v(4.06, 9.85) * mm, "end": v(-4.06, 9.85) * mm});
            skLineSegment(sketch, "E7.1.3.2", {"start": v(4.06, 9.85) * mm, "end": v(4.06, 10.35) * mm});
            skLineSegment(sketch, "E7.1.3.3", {"start": v(-4.06, 9.85) * mm, "end": v(-4.06, 10.35) * mm});
            skLineSegment(sketch, "E7.1.4.0", {"start": v(4.06, 11.35) * mm, "end": v(-4.06, 11.35) * mm});
            skLineSegment(sketch, "E7.1.4.1", {"start": v(4.06, 10.85) * mm, "end": v(-4.06, 10.85) * mm});
            skLineSegment(sketch, "E7.1.4.2", {"start": v(4.06, 10.85) * mm, "end": v(4.06, 11.35) * mm});
            skLineSegment(sketch, "E7.1.4.3", {"start": v(-4.06, 10.85) * mm, "end": v(-4.06, 11.35) * mm});
            skLineSegment(sketch, "E7.1.5.0", {"start": v(4.06, 12.35) * mm, "end": v(-4.06, 12.35) * mm});
            skLineSegment(sketch, "E7.1.5.1", {"start": v(4.06, 11.85) * mm, "end": v(-4.06, 11.85) * mm});
            skLineSegment(sketch, "E7.1.5.2", {"start": v(4.06, 11.85) * mm, "end": v(4.06, 12.35) * mm});
            skLineSegment(sketch, "E7.1.5.3", {"start": v(-4.06, 11.85) * mm, "end": v(-4.06, 12.35) * mm});
            skLineSegment(sketch, "E7.1.6.0", {"start": v(4.06, 13.35) * mm, "end": v(-4.06, 13.35) * mm});
            skLineSegment(sketch, "E7.1.6.1", {"start": v(4.06, 12.85) * mm, "end": v(-4.06, 12.85) * mm});
            skLineSegment(sketch, "E7.1.6.2", {"start": v(4.06, 12.85) * mm, "end": v(4.06, 13.35) * mm});
            skLineSegment(sketch, "E7.1.6.3", {"start": v(-4.06, 12.85) * mm, "end": v(-4.06, 13.35) * mm});
            skLineSegment(sketch, "E7.1.7.0", {"start": v(4.06, 14.35) * mm, "end": v(-4.06, 14.35) * mm});
            skLineSegment(sketch, "E7.1.7.1", {"start": v(4.06, 13.85) * mm, "end": v(-4.06, 13.85) * mm});
            skLineSegment(sketch, "E7.1.7.2", {"start": v(4.06, 13.85) * mm, "end": v(4.06, 14.35) * mm});
            skLineSegment(sketch, "E7.1.7.3", {"start": v(-4.06, 13.85) * mm, "end": v(-4.06, 14.35) * mm});
            skLineSegment(sketch, "E7.1.8.0", {"start": v(4.06, 15.35) * mm, "end": v(-4.06, 15.35) * mm});
            skLineSegment(sketch, "E7.1.8.1", {"start": v(4.06, 14.85) * mm, "end": v(-4.06, 14.85) * mm});
            skLineSegment(sketch, "E7.1.8.2", {"start": v(4.06, 14.85) * mm, "end": v(4.06, 15.35) * mm});
            skLineSegment(sketch, "E7.1.8.3", {"start": v(-4.06, 14.85) * mm, "end": v(-4.06, 15.35) * mm});
            skLineSegment(sketch, "E7.1.9.0", {"start": v(4.06, 16.35) * mm, "end": v(-4.06, 16.35) * mm});
            skLineSegment(sketch, "E7.1.9.1", {"start": v(4.06, 15.85) * mm, "end": v(-4.06, 15.85) * mm});
            skLineSegment(sketch, "E7.1.9.2", {"start": v(4.06, 15.85) * mm, "end": v(4.06, 16.35) * mm});
            skLineSegment(sketch, "E7.1.9.3", {"start": v(-4.06, 15.85) * mm, "end": v(-4.06, 16.35) * mm});
            skLineSegment(sketch, "E7.1.10.0", {"start": v(4.06, 17.35) * mm, "end": v(-4.06, 17.35) * mm});
            skLineSegment(sketch, "E7.1.10.1", {"start": v(4.06, 16.85) * mm, "end": v(-4.06, 16.85) * mm});
            skLineSegment(sketch, "E7.1.10.2", {"start": v(4.06, 16.85) * mm, "end": v(4.06, 17.35) * mm});
            skLineSegment(sketch, "E7.1.10.3", {"start": v(-4.06, 16.85) * mm, "end": v(-4.06, 17.35) * mm});
            skLineSegment(sketch, "E7.1.11.0", {"start": v(4.06, 18.35) * mm, "end": v(-4.06, 18.35) * mm});
            skLineSegment(sketch, "E7.1.11.1", {"start": v(4.06, 17.85) * mm, "end": v(-4.06, 17.85) * mm});
            skLineSegment(sketch, "E7.1.11.2", {"start": v(4.06, 17.85) * mm, "end": v(4.06, 18.35) * mm});
            skLineSegment(sketch, "E7.1.11.3", {"start": v(-4.06, 17.85) * mm, "end": v(-4.06, 18.35) * mm});
            skLineSegment(sketch, "E7.1.12.0", {"start": v(4.06, 19.35) * mm, "end": v(-4.06, 19.35) * mm});
            skLineSegment(sketch, "E7.1.12.1", {"start": v(4.06, 18.85) * mm, "end": v(-4.06, 18.85) * mm});
            skLineSegment(sketch, "E7.1.12.2", {"start": v(4.06, 18.85) * mm, "end": v(4.06, 19.35) * mm});
            skLineSegment(sketch, "E7.1.12.3", {"start": v(-4.06, 18.85) * mm, "end": v(-4.06, 19.35) * mm});
            skLineSegment(sketch, "E7.1.13.0", {"start": v(4.06, 20.35) * mm, "end": v(-4.06, 20.35) * mm});
            skLineSegment(sketch, "E7.1.13.1", {"start": v(4.06, 19.85) * mm, "end": v(-4.06, 19.85) * mm});
            skLineSegment(sketch, "E7.1.13.2", {"start": v(4.06, 19.85) * mm, "end": v(4.06, 20.35) * mm});
            skLineSegment(sketch, "E7.1.13.3", {"start": v(-4.06, 19.85) * mm, "end": v(-4.06, 20.35) * mm});
            skLineSegment(sketch, "E7.1.14.0", {"start": v(4.06, 21.35) * mm, "end": v(-4.06, 21.35) * mm});
            skLineSegment(sketch, "E7.1.14.1", {"start": v(4.06, 20.85) * mm, "end": v(-4.06, 20.85) * mm});
            skLineSegment(sketch, "E7.1.14.2", {"start": v(4.06, 20.85) * mm, "end": v(4.06, 21.35) * mm});
            skLineSegment(sketch, "E7.1.14.3", {"start": v(-4.06, 20.85) * mm, "end": v(-4.06, 21.35) * mm});
            skLineSegment(sketch, "E7.1.15.0", {"start": v(4.06, 22.35) * mm, "end": v(-4.06, 22.35) * mm});
            skLineSegment(sketch, "E7.1.15.1", {"start": v(4.06, 21.85) * mm, "end": v(-4.06, 21.85) * mm});
            skLineSegment(sketch, "E7.1.15.2", {"start": v(4.06, 21.85) * mm, "end": v(4.06, 22.35) * mm});
            skLineSegment(sketch, "E7.1.15.3", {"start": v(-4.06, 21.85) * mm, "end": v(-4.06, 22.35) * mm});
            skLineSegment(sketch, "E7.1.16.0", {"start": v(4.06, 23.35) * mm, "end": v(-4.06, 23.35) * mm});
            skLineSegment(sketch, "E7.1.16.1", {"start": v(4.06, 22.85) * mm, "end": v(-4.06, 22.85) * mm});
            skLineSegment(sketch, "E7.1.16.2", {"start": v(4.06, 22.85) * mm, "end": v(4.06, 23.35) * mm});
            skLineSegment(sketch, "E7.1.16.3", {"start": v(-4.06, 22.85) * mm, "end": v(-4.06, 23.35) * mm});
            skLineSegment(sketch, "E7.1.17.0", {"start": v(4.06, 24.35) * mm, "end": v(-4.06, 24.35) * mm});
            skLineSegment(sketch, "E7.1.17.1", {"start": v(4.06, 23.85) * mm, "end": v(-4.06, 23.85) * mm});
            skLineSegment(sketch, "E7.1.17.2", {"start": v(4.06, 23.85) * mm, "end": v(4.06, 24.35) * mm});
            skLineSegment(sketch, "E7.1.17.3", {"start": v(-4.06, 23.85) * mm, "end": v(-4.06, 24.35) * mm});
            skLineSegment(sketch, "E7.1.18.0", {"start": v(4.06, 25.35) * mm, "end": v(-4.06, 25.35) * mm});
            skLineSegment(sketch, "E7.1.18.1", {"start": v(4.06, 24.85) * mm, "end": v(-4.06, 24.85) * mm});
            skLineSegment(sketch, "E7.1.18.2", {"start": v(4.06, 24.85) * mm, "end": v(4.06, 25.35) * mm});
            skLineSegment(sketch, "E7.1.18.3", {"start": v(-4.06, 24.85) * mm, "end": v(-4.06, 25.35) * mm});
            skLineSegment(sketch, "E7.1.19.0", {"start": v(4.06, 26.35) * mm, "end": v(-4.06, 26.35) * mm});
            skLineSegment(sketch, "E7.1.19.1", {"start": v(4.06, 25.85) * mm, "end": v(-4.06, 25.85) * mm});
            skLineSegment(sketch, "E7.1.19.2", {"start": v(4.06, 25.85) * mm, "end": v(4.06, 26.35) * mm});
            skLineSegment(sketch, "E7.1.19.3", {"start": v(-4.06, 25.85) * mm, "end": v(-4.06, 26.35) * mm});
            skLineSegment(sketch, "E7.1.20.0", {"start": v(4.06, 27.35) * mm, "end": v(-4.06, 27.35) * mm});
            skLineSegment(sketch, "E7.1.20.1", {"start": v(4.06, 26.85) * mm, "end": v(-4.06, 26.85) * mm});
            skLineSegment(sketch, "E7.1.20.2", {"start": v(4.06, 26.85) * mm, "end": v(4.06, 27.35) * mm});
            skLineSegment(sketch, "E7.1.20.3", {"start": v(-4.06, 26.85) * mm, "end": v(-4.06, 27.35) * mm});
            skLineSegment(sketch, "E7.1.21.0", {"start": v(4.06, 28.35) * mm, "end": v(-4.06, 28.35) * mm});
            skLineSegment(sketch, "E7.1.21.1", {"start": v(4.06, 27.85) * mm, "end": v(-4.06, 27.85) * mm});
            skLineSegment(sketch, "E7.1.21.2", {"start": v(4.06, 27.85) * mm, "end": v(4.06, 28.35) * mm});
            skLineSegment(sketch, "E7.1.21.3", {"start": v(-4.06, 27.85) * mm, "end": v(-4.06, 28.35) * mm});
            skLineSegment(sketch, "E7.1.22.0", {"start": v(4.06, 29.35) * mm, "end": v(-4.06, 29.35) * mm});
            skLineSegment(sketch, "E7.1.22.1", {"start": v(4.06, 28.85) * mm, "end": v(-4.06, 28.85) * mm});
            skLineSegment(sketch, "E7.1.22.2", {"start": v(4.06, 28.85) * mm, "end": v(4.06, 29.35) * mm});
            skLineSegment(sketch, "E7.1.22.3", {"start": v(-4.06, 28.85) * mm, "end": v(-4.06, 29.35) * mm});
            skLineSegment(sketch, "E7.1.23.0", {"start": v(4.06, 30.35) * mm, "end": v(-4.06, 30.35) * mm});
            skLineSegment(sketch, "E7.1.23.1", {"start": v(4.06, 29.85) * mm, "end": v(-4.06, 29.85) * mm});
            skLineSegment(sketch, "E7.1.23.2", {"start": v(4.06, 29.85) * mm, "end": v(4.06, 30.35) * mm});
            skLineSegment(sketch, "E7.1.23.3", {"start": v(-4.06, 29.85) * mm, "end": v(-4.06, 30.35) * mm});
            skLineSegment(sketch, "E7.1.24.0", {"start": v(4.06, 31.35) * mm, "end": v(-4.06, 31.35) * mm});
            skLineSegment(sketch, "E7.1.24.1", {"start": v(4.06, 30.85) * mm, "end": v(-4.06, 30.85) * mm});
            skLineSegment(sketch, "E7.1.24.2", {"start": v(4.06, 30.85) * mm, "end": v(4.06, 31.35) * mm});
            skLineSegment(sketch, "E7.1.24.3", {"start": v(-4.06, 30.85) * mm, "end": v(-4.06, 31.35) * mm});
            skLineSegment(sketch, "E7.1.25.0", {"start": v(4.06, 32.35) * mm, "end": v(-4.06, 32.35) * mm});
            skLineSegment(sketch, "E7.1.25.1", {"start": v(4.06, 31.85) * mm, "end": v(-4.06, 31.85) * mm});
            skLineSegment(sketch, "E7.1.25.2", {"start": v(4.06, 31.85) * mm, "end": v(4.06, 32.35) * mm});
            skLineSegment(sketch, "E7.1.25.3", {"start": v(-4.06, 31.85) * mm, "end": v(-4.06, 32.35) * mm});
            skLineSegment(sketch, "E7.1.26.0", {"start": v(4.06, 33.35) * mm, "end": v(-4.06, 33.35) * mm});
            skLineSegment(sketch, "E7.1.26.1", {"start": v(4.06, 32.85) * mm, "end": v(-4.06, 32.85) * mm});
            skLineSegment(sketch, "E7.1.26.2", {"start": v(4.06, 32.85) * mm, "end": v(4.06, 33.35) * mm});
            skLineSegment(sketch, "E7.1.26.3", {"start": v(-4.06, 32.85) * mm, "end": v(-4.06, 33.35) * mm});
            skLineSegment(sketch, "E7.1.27.0", {"start": v(4.06, 34.35) * mm, "end": v(-4.06, 34.35) * mm});
            skLineSegment(sketch, "E7.1.27.1", {"start": v(4.06, 33.85) * mm, "end": v(-4.06, 33.85) * mm});
            skLineSegment(sketch, "E7.1.27.2", {"start": v(4.06, 33.85) * mm, "end": v(4.06, 34.35) * mm});
            skLineSegment(sketch, "E7.1.27.3", {"start": v(-4.06, 33.85) * mm, "end": v(-4.06, 34.35) * mm});
            skLineSegment(sketch, "E7.1.28.0", {"start": v(4.06, 35.35) * mm, "end": v(-4.06, 35.35) * mm});
            skLineSegment(sketch, "E7.1.28.1", {"start": v(4.06, 34.85) * mm, "end": v(-4.06, 34.85) * mm});
            skLineSegment(sketch, "E7.1.28.2", {"start": v(4.06, 34.85) * mm, "end": v(4.06, 35.35) * mm});
            skLineSegment(sketch, "E7.1.28.3", {"start": v(-4.06, 34.85) * mm, "end": v(-4.06, 35.35) * mm});
            skLineSegment(sketch, "E7.1.29.0", {"start": v(4.06, 36.35) * mm, "end": v(-4.06, 36.35) * mm});
            skLineSegment(sketch, "E7.1.29.1", {"start": v(4.06, 35.85) * mm, "end": v(-4.06, 35.85) * mm});
            skLineSegment(sketch, "E7.1.29.2", {"start": v(4.06, 35.85) * mm, "end": v(4.06, 36.35) * mm});
            skLineSegment(sketch, "E7.1.29.3", {"start": v(-4.06, 35.85) * mm, "end": v(-4.06, 36.35) * mm});
            skLineSegment(sketch, "E7.1.30.0", {"start": v(4.06, 37.35) * mm, "end": v(-4.06, 37.35) * mm});
            skLineSegment(sketch, "E7.1.30.1", {"start": v(4.06, 36.85) * mm, "end": v(-4.06, 36.85) * mm});
            skLineSegment(sketch, "E7.1.30.2", {"start": v(4.06, 36.85) * mm, "end": v(4.06, 37.35) * mm});
            skLineSegment(sketch, "E7.1.30.3", {"start": v(-4.06, 36.85) * mm, "end": v(-4.06, 37.35) * mm});
            skLineSegment(sketch, "E7.1.31.0", {"start": v(4.06, 38.35) * mm, "end": v(-4.06, 38.35) * mm});
            skLineSegment(sketch, "E7.1.31.1", {"start": v(4.06, 37.85) * mm, "end": v(-4.06, 37.85) * mm});
            skLineSegment(sketch, "E7.1.31.2", {"start": v(4.06, 37.85) * mm, "end": v(4.06, 38.35) * mm});
            skLineSegment(sketch, "E7.1.31.3", {"start": v(-4.06, 37.85) * mm, "end": v(-4.06, 38.35) * mm});
            skLineSegment(sketch, "E7.1.32.0", {"start": v(4.06, 39.35) * mm, "end": v(-4.06, 39.35) * mm});
            skLineSegment(sketch, "E7.1.32.1", {"start": v(4.06, 38.85) * mm, "end": v(-4.06, 38.85) * mm});
            skLineSegment(sketch, "E7.1.32.2", {"start": v(4.06, 38.85) * mm, "end": v(4.06, 39.35) * mm});
            skLineSegment(sketch, "E7.1.32.3", {"start": v(-4.06, 38.85) * mm, "end": v(-4.06, 39.35) * mm});
            skLineSegment(sketch, "E7.1.33.0", {"start": v(4.06, 40.35) * mm, "end": v(-4.06, 40.35) * mm});
            skLineSegment(sketch, "E7.1.33.1", {"start": v(4.06, 39.85) * mm, "end": v(-4.06, 39.85) * mm});
            skLineSegment(sketch, "E7.1.33.2", {"start": v(4.06, 39.85) * mm, "end": v(4.06, 40.35) * mm});
            skLineSegment(sketch, "E7.1.33.3", {"start": v(-4.06, 39.85) * mm, "end": v(-4.06, 40.35) * mm});
            skLineSegment(sketch, "E7.1.34.0", {"start": v(4.06, 41.35) * mm, "end": v(-4.06, 41.35) * mm});
            skLineSegment(sketch, "E7.1.34.1", {"start": v(4.06, 40.85) * mm, "end": v(-4.06, 40.85) * mm});
            skLineSegment(sketch, "E7.1.34.2", {"start": v(4.06, 40.85) * mm, "end": v(4.06, 41.35) * mm});
            skLineSegment(sketch, "E7.1.34.3", {"start": v(-4.06, 40.85) * mm, "end": v(-4.06, 41.35) * mm});
            skLineSegment(sketch, "E7.1.35.0", {"start": v(4.06, 42.35) * mm, "end": v(-4.06, 42.35) * mm});
            skLineSegment(sketch, "E7.1.35.1", {"start": v(4.06, 41.85) * mm, "end": v(-4.06, 41.85) * mm});
            skLineSegment(sketch, "E7.1.35.2", {"start": v(4.06, 41.85) * mm, "end": v(4.06, 42.35) * mm});
            skLineSegment(sketch, "E7.1.35.3", {"start": v(-4.06, 41.85) * mm, "end": v(-4.06, 42.35) * mm});
            skLineSegment(sketch, "E7.1.36.0", {"start": v(4.06, 43.35) * mm, "end": v(-4.06, 43.35) * mm});
            skLineSegment(sketch, "E7.1.36.1", {"start": v(4.06, 42.85) * mm, "end": v(-4.06, 42.85) * mm});
            skLineSegment(sketch, "E7.1.36.2", {"start": v(4.06, 42.85) * mm, "end": v(4.06, 43.35) * mm});
            skLineSegment(sketch, "E7.1.36.3", {"start": v(-4.06, 42.85) * mm, "end": v(-4.06, 43.35) * mm});
            skLineSegment(sketch, "E7.1.37.0", {"start": v(4.06, 44.35) * mm, "end": v(-4.06, 44.35) * mm});
            skLineSegment(sketch, "E7.1.37.1", {"start": v(4.06, 43.85) * mm, "end": v(-4.06, 43.85) * mm});
            skLineSegment(sketch, "E7.1.37.2", {"start": v(4.06, 43.85) * mm, "end": v(4.06, 44.35) * mm});
            skLineSegment(sketch, "E7.1.37.3", {"start": v(-4.06, 43.85) * mm, "end": v(-4.06, 44.35) * mm});
            skLineSegment(sketch, "E7.1.38.0", {"start": v(4.06, 45.35) * mm, "end": v(-4.06, 45.35) * mm});
            skLineSegment(sketch, "E7.1.38.1", {"start": v(4.06, 44.85) * mm, "end": v(-4.06, 44.85) * mm});
            skLineSegment(sketch, "E7.1.38.2", {"start": v(4.06, 44.85) * mm, "end": v(4.06, 45.35) * mm});
            skLineSegment(sketch, "E7.1.38.3", {"start": v(-4.06, 44.85) * mm, "end": v(-4.06, 45.35) * mm});
            skLineSegment(sketch, "E7.1.39.0", {"start": v(4.06, 46.35) * mm, "end": v(-4.06, 46.35) * mm});
            skLineSegment(sketch, "E7.1.39.1", {"start": v(4.06, 45.85) * mm, "end": v(-4.06, 45.85) * mm});
            skLineSegment(sketch, "E7.1.39.2", {"start": v(4.06, 45.85) * mm, "end": v(4.06, 46.35) * mm});
            skLineSegment(sketch, "E7.1.39.3", {"start": v(-4.06, 45.85) * mm, "end": v(-4.06, 46.35) * mm});
            skLineSegment(sketch, "E7.1.40.0", {"start": v(4.06, 47.35) * mm, "end": v(-4.06, 47.35) * mm});
            skLineSegment(sketch, "E7.1.40.1", {"start": v(4.06, 46.85) * mm, "end": v(-4.06, 46.85) * mm});
            skLineSegment(sketch, "E7.1.40.2", {"start": v(4.06, 46.85) * mm, "end": v(4.06, 47.35) * mm});
            skLineSegment(sketch, "E7.1.40.3", {"start": v(-4.06, 46.85) * mm, "end": v(-4.06, 47.35) * mm});
            skLineSegment(sketch, "E7.1.41.0", {"start": v(4.06, 48.35) * mm, "end": v(-4.06, 48.35) * mm});
            skLineSegment(sketch, "E7.1.41.1", {"start": v(4.06, 47.85) * mm, "end": v(-4.06, 47.85) * mm});
            skLineSegment(sketch, "E7.1.41.2", {"start": v(4.06, 47.85) * mm, "end": v(4.06, 48.35) * mm});
            skLineSegment(sketch, "E7.1.41.3", {"start": v(-4.06, 47.85) * mm, "end": v(-4.06, 48.35) * mm});
            skLineSegment(sketch, "E7.1.42.0", {"start": v(4.06, 49.35) * mm, "end": v(-4.06, 49.35) * mm});
            skLineSegment(sketch, "E7.1.42.1", {"start": v(4.06, 48.85) * mm, "end": v(-4.06, 48.85) * mm});
            skLineSegment(sketch, "E7.1.42.2", {"start": v(4.06, 48.85) * mm, "end": v(4.06, 49.35) * mm});
            skLineSegment(sketch, "E7.1.42.3", {"start": v(-4.06, 48.85) * mm, "end": v(-4.06, 49.35) * mm});
            skLineSegment(sketch, "E7.1.43.0", {"start": v(4.06, 50.35) * mm, "end": v(-4.06, 50.35) * mm});
            skLineSegment(sketch, "E7.1.43.1", {"start": v(4.06, 49.85) * mm, "end": v(-4.06, 49.85) * mm});
            skLineSegment(sketch, "E7.1.43.2", {"start": v(4.06, 49.85) * mm, "end": v(4.06, 50.35) * mm});
            skLineSegment(sketch, "E7.1.43.3", {"start": v(-4.06, 49.85) * mm, "end": v(-4.06, 50.35) * mm});
            skLineSegment(sketch, "E7.1.44.0", {"start": v(4.06, 51.35) * mm, "end": v(-4.06, 51.35) * mm});
            skLineSegment(sketch, "E7.1.44.1", {"start": v(4.06, 50.85) * mm, "end": v(-4.06, 50.85) * mm});
            skLineSegment(sketch, "E7.1.44.2", {"start": v(4.06, 50.85) * mm, "end": v(4.06, 51.35) * mm});
            skLineSegment(sketch, "E7.1.44.3", {"start": v(-4.06, 50.85) * mm, "end": v(-4.06, 51.35) * mm});
            skLineSegment(sketch, "E7.1.45.0", {"start": v(4.06, 52.35) * mm, "end": v(-4.06, 52.35) * mm});
            skLineSegment(sketch, "E7.1.45.1", {"start": v(4.06, 51.85) * mm, "end": v(-4.06, 51.85) * mm});
            skLineSegment(sketch, "E7.1.45.2", {"start": v(4.06, 51.85) * mm, "end": v(4.06, 52.35) * mm});
            skLineSegment(sketch, "E7.1.45.3", {"start": v(-4.06, 51.85) * mm, "end": v(-4.06, 52.35) * mm});
            skLineSegment(sketch, "E7.1.46.0", {"start": v(4.06, 53.35) * mm, "end": v(-4.06, 53.35) * mm});
            skLineSegment(sketch, "E7.1.46.1", {"start": v(4.06, 52.85) * mm, "end": v(-4.06, 52.85) * mm});
            skLineSegment(sketch, "E7.1.46.2", {"start": v(4.06, 52.85) * mm, "end": v(4.06, 53.35) * mm});
            skLineSegment(sketch, "E7.1.46.3", {"start": v(-4.06, 52.85) * mm, "end": v(-4.06, 53.35) * mm});
            skLineSegment(sketch, "E7.1.47.0", {"start": v(4.06, 54.35) * mm, "end": v(-4.06, 54.35) * mm});
            skLineSegment(sketch, "E7.1.47.1", {"start": v(4.06, 53.85) * mm, "end": v(-4.06, 53.85) * mm});
            skLineSegment(sketch, "E7.1.47.2", {"start": v(4.06, 53.85) * mm, "end": v(4.06, 54.35) * mm});
            skLineSegment(sketch, "E7.1.47.3", {"start": v(-4.06, 53.85) * mm, "end": v(-4.06, 54.35) * mm});
            skLineSegment(sketch, "E7.1.48.0", {"start": v(4.06, 55.35) * mm, "end": v(-4.06, 55.35) * mm});
            skLineSegment(sketch, "E7.1.48.1", {"start": v(4.06, 54.85) * mm, "end": v(-4.06, 54.85) * mm});
            skLineSegment(sketch, "E7.1.48.2", {"start": v(4.06, 54.85) * mm, "end": v(4.06, 55.35) * mm});
            skLineSegment(sketch, "E7.1.48.3", {"start": v(-4.06, 54.85) * mm, "end": v(-4.06, 55.35) * mm});
            skLineSegment(sketch, "E7.1.49.0", {"start": v(4.06, 56.35) * mm, "end": v(-4.06, 56.35) * mm});
            skLineSegment(sketch, "E7.1.49.1", {"start": v(4.06, 55.85) * mm, "end": v(-4.06, 55.85) * mm});
            skLineSegment(sketch, "E7.1.49.2", {"start": v(4.06, 55.85) * mm, "end": v(4.06, 56.35) * mm});
            skLineSegment(sketch, "E7.1.49.3", {"start": v(-4.06, 55.85) * mm, "end": v(-4.06, 56.35) * mm});
            skLineSegment(sketch, "E7.1.50.0", {"start": v(4.06, 57.35) * mm, "end": v(-4.06, 57.35) * mm});
            skLineSegment(sketch, "E7.1.50.1", {"start": v(4.06, 56.85) * mm, "end": v(-4.06, 56.85) * mm});
            skLineSegment(sketch, "E7.1.50.2", {"start": v(4.06, 56.85) * mm, "end": v(4.06, 57.35) * mm});
            skLineSegment(sketch, "E7.1.50.3", {"start": v(-4.06, 56.85) * mm, "end": v(-4.06, 57.35) * mm});
            skLineSegment(sketch, "E7.1.51.0", {"start": v(4.06, 58.35) * mm, "end": v(-4.06, 58.35) * mm});
            skLineSegment(sketch, "E7.1.51.1", {"start": v(4.06, 57.85) * mm, "end": v(-4.06, 57.85) * mm});
            skLineSegment(sketch, "E7.1.51.2", {"start": v(4.06, 57.85) * mm, "end": v(4.06, 58.35) * mm});
            skLineSegment(sketch, "E7.1.51.3", {"start": v(-4.06, 57.85) * mm, "end": v(-4.06, 58.35) * mm});
            skLineSegment(sketch, "E7.1.52.0", {"start": v(4.06, 59.35) * mm, "end": v(-4.06, 59.35) * mm});
            skLineSegment(sketch, "E7.1.52.1", {"start": v(4.06, 58.85) * mm, "end": v(-4.06, 58.85) * mm});
            skLineSegment(sketch, "E7.1.52.2", {"start": v(4.06, 58.85) * mm, "end": v(4.06, 59.35) * mm});
            skLineSegment(sketch, "E7.1.52.3", {"start": v(-4.06, 58.85) * mm, "end": v(-4.06, 59.35) * mm});
            skLineSegment(sketch, "E7.1.53.0", {"start": v(4.06, 60.35) * mm, "end": v(-4.06, 60.35) * mm});
            skLineSegment(sketch, "E7.1.53.1", {"start": v(4.06, 59.85) * mm, "end": v(-4.06, 59.85) * mm});
            skLineSegment(sketch, "E7.1.53.2", {"start": v(4.06, 59.85) * mm, "end": v(4.06, 60.35) * mm});
            skLineSegment(sketch, "E7.1.53.3", {"start": v(-4.06, 59.85) * mm, "end": v(-4.06, 60.35) * mm});
            skLineSegment(sketch, "E7.1.54.0", {"start": v(4.06, 61.35) * mm, "end": v(-4.06, 61.35) * mm});
            skLineSegment(sketch, "E7.1.54.1", {"start": v(4.06, 60.85) * mm, "end": v(-4.06, 60.85) * mm});
            skLineSegment(sketch, "E7.1.54.2", {"start": v(4.06, 60.85) * mm, "end": v(4.06, 61.35) * mm});
            skLineSegment(sketch, "E7.1.54.3", {"start": v(-4.06, 60.85) * mm, "end": v(-4.06, 61.35) * mm});
            skLineSegment(sketch, "E7.1.55.0", {"start": v(4.06, 62.35) * mm, "end": v(-4.06, 62.35) * mm});
            skLineSegment(sketch, "E7.1.55.1", {"start": v(4.06, 61.85) * mm, "end": v(-4.06, 61.85) * mm});
            skLineSegment(sketch, "E7.1.55.2", {"start": v(4.06, 61.85) * mm, "end": v(4.06, 62.35) * mm});
            skLineSegment(sketch, "E7.1.55.3", {"start": v(-4.06, 61.85) * mm, "end": v(-4.06, 62.35) * mm});
            skLineSegment(sketch, "E7.1.56.0", {"start": v(4.06, 63.35) * mm, "end": v(-4.06, 63.35) * mm});
            skLineSegment(sketch, "E7.1.56.1", {"start": v(4.06, 62.85) * mm, "end": v(-4.06, 62.85) * mm});
            skLineSegment(sketch, "E7.1.56.2", {"start": v(4.06, 62.85) * mm, "end": v(4.06, 63.35) * mm});
            skLineSegment(sketch, "E7.1.56.3", {"start": v(-4.06, 62.85) * mm, "end": v(-4.06, 63.35) * mm});
            skLineSegment(sketch, "E7.1.57.0", {"start": v(4.06, 64.35) * mm, "end": v(-4.06, 64.35) * mm});
            skLineSegment(sketch, "E7.1.57.1", {"start": v(4.06, 63.85) * mm, "end": v(-4.06, 63.85) * mm});
            skLineSegment(sketch, "E7.1.57.2", {"start": v(4.06, 63.85) * mm, "end": v(4.06, 64.35) * mm});
            skLineSegment(sketch, "E7.1.57.3", {"start": v(-4.06, 63.85) * mm, "end": v(-4.06, 64.35) * mm});
            skLineSegment(sketch, "E7.1.58.0", {"start": v(4.06, 65.35) * mm, "end": v(-4.06, 65.35) * mm});
            skLineSegment(sketch, "E7.1.58.1", {"start": v(4.06, 64.85) * mm, "end": v(-4.06, 64.85) * mm});
            skLineSegment(sketch, "E7.1.58.2", {"start": v(4.06, 64.85) * mm, "end": v(4.06, 65.35) * mm});
            skLineSegment(sketch, "E7.1.58.3", {"start": v(-4.06, 64.85) * mm, "end": v(-4.06, 65.35) * mm});
            skLineSegment(sketch, "E7.1.59.0", {"start": v(4.06, 66.35) * mm, "end": v(-4.06, 66.35) * mm});
            skLineSegment(sketch, "E7.1.59.1", {"start": v(4.06, 65.85) * mm, "end": v(-4.06, 65.85) * mm});
            skLineSegment(sketch, "E7.1.59.2", {"start": v(4.06, 65.85) * mm, "end": v(4.06, 66.35) * mm});
            skLineSegment(sketch, "E7.1.59.3", {"start": v(-4.06, 65.85) * mm, "end": v(-4.06, 66.35) * mm});
            skLineSegment(sketch, "E7.1.60.0", {"start": v(4.06, 67.35) * mm, "end": v(-4.06, 67.35) * mm});
            skLineSegment(sketch, "E7.1.60.1", {"start": v(4.06, 66.85) * mm, "end": v(-4.06, 66.85) * mm});
            skLineSegment(sketch, "E7.1.60.2", {"start": v(4.06, 66.85) * mm, "end": v(4.06, 67.35) * mm});
            skLineSegment(sketch, "E7.1.60.3", {"start": v(-4.06, 66.85) * mm, "end": v(-4.06, 67.35) * mm});
            skLineSegment(sketch, "E7.1.61.0", {"start": v(4.06, 68.35) * mm, "end": v(-4.06, 68.35) * mm});
            skLineSegment(sketch, "E7.1.61.1", {"start": v(4.06, 67.85) * mm, "end": v(-4.06, 67.85) * mm});
            skLineSegment(sketch, "E7.1.61.2", {"start": v(4.06, 67.85) * mm, "end": v(4.06, 68.35) * mm});
            skLineSegment(sketch, "E7.1.61.3", {"start": v(-4.06, 67.85) * mm, "end": v(-4.06, 68.35) * mm});
            skLineSegment(sketch, "E7.1.62.0", {"start": v(4.06, 69.35) * mm, "end": v(-4.06, 69.35) * mm});
            skLineSegment(sketch, "E7.1.62.1", {"start": v(4.06, 68.85) * mm, "end": v(-4.06, 68.85) * mm});
            skLineSegment(sketch, "E7.1.62.2", {"start": v(4.06, 68.85) * mm, "end": v(4.06, 69.35) * mm});
            skLineSegment(sketch, "E7.1.62.3", {"start": v(-4.06, 68.85) * mm, "end": v(-4.06, 69.35) * mm});
            skLineSegment(sketch, "E7.1.63.0", {"start": v(4.06, 70.35) * mm, "end": v(-4.06, 70.35) * mm});
            skLineSegment(sketch, "E7.1.63.1", {"start": v(4.06, 69.85) * mm, "end": v(-4.06, 69.85) * mm});
            skLineSegment(sketch, "E7.1.63.2", {"start": v(4.06, 69.85) * mm, "end": v(4.06, 70.35) * mm});
            skLineSegment(sketch, "E7.1.63.3", {"start": v(-4.06, 69.85) * mm, "end": v(-4.06, 70.35) * mm});
            skLineSegment(sketch, "E7.1.64.0", {"start": v(4.06, 71.35) * mm, "end": v(-4.06, 71.35) * mm});
            skLineSegment(sketch, "E7.1.64.1", {"start": v(4.06, 70.85) * mm, "end": v(-4.06, 70.85) * mm});
            skLineSegment(sketch, "E7.1.64.2", {"start": v(4.06, 70.85) * mm, "end": v(4.06, 71.35) * mm});
            skLineSegment(sketch, "E7.1.64.3", {"start": v(-4.06, 70.85) * mm, "end": v(-4.06, 71.35) * mm});
            skLineSegment(sketch, "E7.1.65.0", {"start": v(4.06, 72.35) * mm, "end": v(-4.06, 72.35) * mm});
            skLineSegment(sketch, "E7.1.65.1", {"start": v(4.06, 71.85) * mm, "end": v(-4.06, 71.85) * mm});
            skLineSegment(sketch, "E7.1.65.2", {"start": v(4.06, 71.85) * mm, "end": v(4.06, 72.35) * mm});
            skLineSegment(sketch, "E7.1.65.3", {"start": v(-4.06, 71.85) * mm, "end": v(-4.06, 72.35) * mm});
            skLineSegment(sketch, "E7.1.66.0", {"start": v(4.06, 73.35) * mm, "end": v(-4.06, 73.35) * mm});
            skLineSegment(sketch, "E7.1.66.1", {"start": v(4.06, 72.85) * mm, "end": v(-4.06, 72.85) * mm});
            skLineSegment(sketch, "E7.1.66.2", {"start": v(4.06, 72.85) * mm, "end": v(4.06, 73.35) * mm});
            skLineSegment(sketch, "E7.1.66.3", {"start": v(-4.06, 72.85) * mm, "end": v(-4.06, 73.35) * mm});
            skLineSegment(sketch, "E7.1.67.0", {"start": v(4.06, 74.35) * mm, "end": v(-4.06, 74.35) * mm});
            skLineSegment(sketch, "E7.1.67.1", {"start": v(4.06, 73.85) * mm, "end": v(-4.06, 73.85) * mm});
            skLineSegment(sketch, "E7.1.67.2", {"start": v(4.06, 73.85) * mm, "end": v(4.06, 74.35) * mm});
            skLineSegment(sketch, "E7.1.67.3", {"start": v(-4.06, 73.85) * mm, "end": v(-4.06, 74.35) * mm});
            skLineSegment(sketch, "E7.1.68.0", {"start": v(4.06, 75.35) * mm, "end": v(-4.06, 75.35) * mm});
            skLineSegment(sketch, "E7.1.68.1", {"start": v(4.06, 74.85) * mm, "end": v(-4.06, 74.85) * mm});
            skLineSegment(sketch, "E7.1.68.2", {"start": v(4.06, 74.85) * mm, "end": v(4.06, 75.35) * mm});
            skLineSegment(sketch, "E7.1.68.3", {"start": v(-4.06, 74.85) * mm, "end": v(-4.06, 75.35) * mm});
            skLineSegment(sketch, "E7.2.0.0", {"start": v(26.72, 7.35) * mm, "end": v(18.6, 7.35) * mm});
            skLineSegment(sketch, "E7.2.0.1", {"start": v(26.72, 6.85) * mm, "end": v(18.6, 6.85) * mm});
            skLineSegment(sketch, "E7.2.0.2", {"start": v(26.72, 6.85) * mm, "end": v(26.72, 7.35) * mm});
            skLineSegment(sketch, "E7.2.0.3", {"start": v(18.6, 6.85) * mm, "end": v(18.6, 7.35) * mm});
            skLineSegment(sketch, "E7.2.1.0", {"start": v(26.72, 8.35) * mm, "end": v(18.6, 8.35) * mm});
            skLineSegment(sketch, "E7.2.1.1", {"start": v(26.72, 7.85) * mm, "end": v(18.6, 7.85) * mm});
            skLineSegment(sketch, "E7.2.1.2", {"start": v(26.72, 7.85) * mm, "end": v(26.72, 8.35) * mm});
            skLineSegment(sketch, "E7.2.1.3", {"start": v(18.6, 7.85) * mm, "end": v(18.6, 8.35) * mm});
            skLineSegment(sketch, "E7.2.2.0", {"start": v(26.72, 9.35) * mm, "end": v(18.6, 9.35) * mm});
            skLineSegment(sketch, "E7.2.2.1", {"start": v(26.72, 8.85) * mm, "end": v(18.6, 8.85) * mm});
            skLineSegment(sketch, "E7.2.2.2", {"start": v(26.72, 8.85) * mm, "end": v(26.72, 9.35) * mm});
            skLineSegment(sketch, "E7.2.2.3", {"start": v(18.6, 8.85) * mm, "end": v(18.6, 9.35) * mm});
            skLineSegment(sketch, "E7.2.3.0", {"start": v(26.72, 10.35) * mm, "end": v(18.6, 10.35) * mm});
            skLineSegment(sketch, "E7.2.3.1", {"start": v(26.72, 9.85) * mm, "end": v(18.6, 9.85) * mm});
            skLineSegment(sketch, "E7.2.3.2", {"start": v(26.72, 9.85) * mm, "end": v(26.72, 10.35) * mm});
            skLineSegment(sketch, "E7.2.3.3", {"start": v(18.6, 9.85) * mm, "end": v(18.6, 10.35) * mm});
            skLineSegment(sketch, "E7.2.4.0", {"start": v(26.72, 11.35) * mm, "end": v(18.6, 11.35) * mm});
            skLineSegment(sketch, "E7.2.4.1", {"start": v(26.72, 10.85) * mm, "end": v(18.6, 10.85) * mm});
            skLineSegment(sketch, "E7.2.4.2", {"start": v(26.72, 10.85) * mm, "end": v(26.72, 11.35) * mm});
            skLineSegment(sketch, "E7.2.4.3", {"start": v(18.6, 10.85) * mm, "end": v(18.6, 11.35) * mm});
            skLineSegment(sketch, "E7.2.5.0", {"start": v(26.72, 12.35) * mm, "end": v(18.6, 12.35) * mm});
            skLineSegment(sketch, "E7.2.5.1", {"start": v(26.72, 11.85) * mm, "end": v(18.6, 11.85) * mm});
            skLineSegment(sketch, "E7.2.5.2", {"start": v(26.72, 11.85) * mm, "end": v(26.72, 12.35) * mm});
            skLineSegment(sketch, "E7.2.5.3", {"start": v(18.6, 11.85) * mm, "end": v(18.6, 12.35) * mm});
            skLineSegment(sketch, "E7.2.6.0", {"start": v(26.72, 13.35) * mm, "end": v(18.6, 13.35) * mm});
            skLineSegment(sketch, "E7.2.6.1", {"start": v(26.72, 12.85) * mm, "end": v(18.6, 12.85) * mm});
            skLineSegment(sketch, "E7.2.6.2", {"start": v(26.72, 12.85) * mm, "end": v(26.72, 13.35) * mm});
            skLineSegment(sketch, "E7.2.6.3", {"start": v(18.6, 12.85) * mm, "end": v(18.6, 13.35) * mm});
            skLineSegment(sketch, "E7.2.7.0", {"start": v(26.72, 14.35) * mm, "end": v(18.6, 14.35) * mm});
            skLineSegment(sketch, "E7.2.7.1", {"start": v(26.72, 13.85) * mm, "end": v(18.6, 13.85) * mm});
            skLineSegment(sketch, "E7.2.7.2", {"start": v(26.72, 13.85) * mm, "end": v(26.72, 14.35) * mm});
            skLineSegment(sketch, "E7.2.7.3", {"start": v(18.6, 13.85) * mm, "end": v(18.6, 14.35) * mm});
            skLineSegment(sketch, "E7.2.8.0", {"start": v(26.72, 15.35) * mm, "end": v(18.6, 15.35) * mm});
            skLineSegment(sketch, "E7.2.8.1", {"start": v(26.72, 14.85) * mm, "end": v(18.6, 14.85) * mm});
            skLineSegment(sketch, "E7.2.8.2", {"start": v(26.72, 14.85) * mm, "end": v(26.72, 15.35) * mm});
            skLineSegment(sketch, "E7.2.8.3", {"start": v(18.6, 14.85) * mm, "end": v(18.6, 15.35) * mm});
            skLineSegment(sketch, "E7.2.9.0", {"start": v(26.72, 16.35) * mm, "end": v(18.6, 16.35) * mm});
            skLineSegment(sketch, "E7.2.9.1", {"start": v(26.72, 15.85) * mm, "end": v(18.6, 15.85) * mm});
            skLineSegment(sketch, "E7.2.9.2", {"start": v(26.72, 15.85) * mm, "end": v(26.72, 16.35) * mm});
            skLineSegment(sketch, "E7.2.9.3", {"start": v(18.6, 15.85) * mm, "end": v(18.6, 16.35) * mm});
            skLineSegment(sketch, "E7.2.10.0", {"start": v(26.72, 17.35) * mm, "end": v(18.6, 17.35) * mm});
            skLineSegment(sketch, "E7.2.10.1", {"start": v(26.72, 16.85) * mm, "end": v(18.6, 16.85) * mm});
            skLineSegment(sketch, "E7.2.10.2", {"start": v(26.72, 16.85) * mm, "end": v(26.72, 17.35) * mm});
            skLineSegment(sketch, "E7.2.10.3", {"start": v(18.6, 16.85) * mm, "end": v(18.6, 17.35) * mm});
            skLineSegment(sketch, "E7.2.11.0", {"start": v(26.72, 18.35) * mm, "end": v(18.6, 18.35) * mm});
            skLineSegment(sketch, "E7.2.11.1", {"start": v(26.72, 17.85) * mm, "end": v(18.6, 17.85) * mm});
            skLineSegment(sketch, "E7.2.11.2", {"start": v(26.72, 17.85) * mm, "end": v(26.72, 18.35) * mm});
            skLineSegment(sketch, "E7.2.11.3", {"start": v(18.6, 17.85) * mm, "end": v(18.6, 18.35) * mm});
            skLineSegment(sketch, "E7.2.12.0", {"start": v(26.72, 19.35) * mm, "end": v(18.6, 19.35) * mm});
            skLineSegment(sketch, "E7.2.12.1", {"start": v(26.72, 18.85) * mm, "end": v(18.6, 18.85) * mm});
            skLineSegment(sketch, "E7.2.12.2", {"start": v(26.72, 18.85) * mm, "end": v(26.72, 19.35) * mm});
            skLineSegment(sketch, "E7.2.12.3", {"start": v(18.6, 18.85) * mm, "end": v(18.6, 19.35) * mm});
            skLineSegment(sketch, "E7.2.13.0", {"start": v(26.72, 20.35) * mm, "end": v(18.6, 20.35) * mm});
            skLineSegment(sketch, "E7.2.13.1", {"start": v(26.72, 19.85) * mm, "end": v(18.6, 19.85) * mm});
            skLineSegment(sketch, "E7.2.13.2", {"start": v(26.72, 19.85) * mm, "end": v(26.72, 20.35) * mm});
            skLineSegment(sketch, "E7.2.13.3", {"start": v(18.6, 19.85) * mm, "end": v(18.6, 20.35) * mm});
            skLineSegment(sketch, "E7.2.14.0", {"start": v(26.72, 21.35) * mm, "end": v(18.6, 21.35) * mm});
            skLineSegment(sketch, "E7.2.14.1", {"start": v(26.72, 20.85) * mm, "end": v(18.6, 20.85) * mm});
            skLineSegment(sketch, "E7.2.14.2", {"start": v(26.72, 20.85) * mm, "end": v(26.72, 21.35) * mm});
            skLineSegment(sketch, "E7.2.14.3", {"start": v(18.6, 20.85) * mm, "end": v(18.6, 21.35) * mm});
            skLineSegment(sketch, "E7.2.15.0", {"start": v(26.72, 22.35) * mm, "end": v(18.6, 22.35) * mm});
            skLineSegment(sketch, "E7.2.15.1", {"start": v(26.72, 21.85) * mm, "end": v(18.6, 21.85) * mm});
            skLineSegment(sketch, "E7.2.15.2", {"start": v(26.72, 21.85) * mm, "end": v(26.72, 22.35) * mm});
            skLineSegment(sketch, "E7.2.15.3", {"start": v(18.6, 21.85) * mm, "end": v(18.6, 22.35) * mm});
            skLineSegment(sketch, "E7.2.16.0", {"start": v(26.72, 23.35) * mm, "end": v(18.6, 23.35) * mm});
            skLineSegment(sketch, "E7.2.16.1", {"start": v(26.72, 22.85) * mm, "end": v(18.6, 22.85) * mm});
            skLineSegment(sketch, "E7.2.16.2", {"start": v(26.72, 22.85) * mm, "end": v(26.72, 23.35) * mm});
            skLineSegment(sketch, "E7.2.16.3", {"start": v(18.6, 22.85) * mm, "end": v(18.6, 23.35) * mm});
            skLineSegment(sketch, "E7.2.17.0", {"start": v(26.72, 24.35) * mm, "end": v(18.6, 24.35) * mm});
            skLineSegment(sketch, "E7.2.17.1", {"start": v(26.72, 23.85) * mm, "end": v(18.6, 23.85) * mm});
            skLineSegment(sketch, "E7.2.17.2", {"start": v(26.72, 23.85) * mm, "end": v(26.72, 24.35) * mm});
            skLineSegment(sketch, "E7.2.17.3", {"start": v(18.6, 23.85) * mm, "end": v(18.6, 24.35) * mm});
            skLineSegment(sketch, "E7.2.18.0", {"start": v(26.72, 25.35) * mm, "end": v(18.6, 25.35) * mm});
            skLineSegment(sketch, "E7.2.18.1", {"start": v(26.72, 24.85) * mm, "end": v(18.6, 24.85) * mm});
            skLineSegment(sketch, "E7.2.18.2", {"start": v(26.72, 24.85) * mm, "end": v(26.72, 25.35) * mm});
            skLineSegment(sketch, "E7.2.18.3", {"start": v(18.6, 24.85) * mm, "end": v(18.6, 25.35) * mm});
            skLineSegment(sketch, "E7.2.19.0", {"start": v(26.72, 26.35) * mm, "end": v(18.6, 26.35) * mm});
            skLineSegment(sketch, "E7.2.19.1", {"start": v(26.72, 25.85) * mm, "end": v(18.6, 25.85) * mm});
            skLineSegment(sketch, "E7.2.19.2", {"start": v(26.72, 25.85) * mm, "end": v(26.72, 26.35) * mm});
            skLineSegment(sketch, "E7.2.19.3", {"start": v(18.6, 25.85) * mm, "end": v(18.6, 26.35) * mm});
            skLineSegment(sketch, "E7.2.20.0", {"start": v(26.72, 27.35) * mm, "end": v(18.6, 27.35) * mm});
            skLineSegment(sketch, "E7.2.20.1", {"start": v(26.72, 26.85) * mm, "end": v(18.6, 26.85) * mm});
            skLineSegment(sketch, "E7.2.20.2", {"start": v(26.72, 26.85) * mm, "end": v(26.72, 27.35) * mm});
            skLineSegment(sketch, "E7.2.20.3", {"start": v(18.6, 26.85) * mm, "end": v(18.6, 27.35) * mm});
            skLineSegment(sketch, "E7.2.21.0", {"start": v(26.72, 28.35) * mm, "end": v(18.6, 28.35) * mm});
            skLineSegment(sketch, "E7.2.21.1", {"start": v(26.72, 27.85) * mm, "end": v(18.6, 27.85) * mm});
            skLineSegment(sketch, "E7.2.21.2", {"start": v(26.72, 27.85) * mm, "end": v(26.72, 28.35) * mm});
            skLineSegment(sketch, "E7.2.21.3", {"start": v(18.6, 27.85) * mm, "end": v(18.6, 28.35) * mm});
            skLineSegment(sketch, "E7.2.22.0", {"start": v(26.72, 29.35) * mm, "end": v(18.6, 29.35) * mm});
            skLineSegment(sketch, "E7.2.22.1", {"start": v(26.72, 28.85) * mm, "end": v(18.6, 28.85) * mm});
            skLineSegment(sketch, "E7.2.22.2", {"start": v(26.72, 28.85) * mm, "end": v(26.72, 29.35) * mm});
            skLineSegment(sketch, "E7.2.22.3", {"start": v(18.6, 28.85) * mm, "end": v(18.6, 29.35) * mm});
            skLineSegment(sketch, "E7.2.23.0", {"start": v(26.72, 30.35) * mm, "end": v(18.6, 30.35) * mm});
            skLineSegment(sketch, "E7.2.23.1", {"start": v(26.72, 29.85) * mm, "end": v(18.6, 29.85) * mm});
            skLineSegment(sketch, "E7.2.23.2", {"start": v(26.72, 29.85) * mm, "end": v(26.72, 30.35) * mm});
            skLineSegment(sketch, "E7.2.23.3", {"start": v(18.6, 29.85) * mm, "end": v(18.6, 30.35) * mm});
            skLineSegment(sketch, "E7.2.24.0", {"start": v(26.72, 31.35) * mm, "end": v(18.6, 31.35) * mm});
            skLineSegment(sketch, "E7.2.24.1", {"start": v(26.72, 30.85) * mm, "end": v(18.6, 30.85) * mm});
            skLineSegment(sketch, "E7.2.24.2", {"start": v(26.72, 30.85) * mm, "end": v(26.72, 31.35) * mm});
            skLineSegment(sketch, "E7.2.24.3", {"start": v(18.6, 30.85) * mm, "end": v(18.6, 31.35) * mm});
            skLineSegment(sketch, "E7.2.25.0", {"start": v(26.72, 32.35) * mm, "end": v(18.6, 32.35) * mm});
            skLineSegment(sketch, "E7.2.25.1", {"start": v(26.72, 31.85) * mm, "end": v(18.6, 31.85) * mm});
            skLineSegment(sketch, "E7.2.25.2", {"start": v(26.72, 31.85) * mm, "end": v(26.72, 32.35) * mm});
            skLineSegment(sketch, "E7.2.25.3", {"start": v(18.6, 31.85) * mm, "end": v(18.6, 32.35) * mm});
            skLineSegment(sketch, "E7.2.26.0", {"start": v(26.72, 33.35) * mm, "end": v(18.6, 33.35) * mm});
            skLineSegment(sketch, "E7.2.26.1", {"start": v(26.72, 32.85) * mm, "end": v(18.6, 32.85) * mm});
            skLineSegment(sketch, "E7.2.26.2", {"start": v(26.72, 32.85) * mm, "end": v(26.72, 33.35) * mm});
            skLineSegment(sketch, "E7.2.26.3", {"start": v(18.6, 32.85) * mm, "end": v(18.6, 33.35) * mm});
            skLineSegment(sketch, "E7.2.27.0", {"start": v(26.72, 34.35) * mm, "end": v(18.6, 34.35) * mm});
            skLineSegment(sketch, "E7.2.27.1", {"start": v(26.72, 33.85) * mm, "end": v(18.6, 33.85) * mm});
            skLineSegment(sketch, "E7.2.27.2", {"start": v(26.72, 33.85) * mm, "end": v(26.72, 34.35) * mm});
            skLineSegment(sketch, "E7.2.27.3", {"start": v(18.6, 33.85) * mm, "end": v(18.6, 34.35) * mm});
            skLineSegment(sketch, "E7.2.28.0", {"start": v(26.72, 35.35) * mm, "end": v(18.6, 35.35) * mm});
            skLineSegment(sketch, "E7.2.28.1", {"start": v(26.72, 34.85) * mm, "end": v(18.6, 34.85) * mm});
            skLineSegment(sketch, "E7.2.28.2", {"start": v(26.72, 34.85) * mm, "end": v(26.72, 35.35) * mm});
            skLineSegment(sketch, "E7.2.28.3", {"start": v(18.6, 34.85) * mm, "end": v(18.6, 35.35) * mm});
            skLineSegment(sketch, "E7.2.29.0", {"start": v(26.72, 36.35) * mm, "end": v(18.6, 36.35) * mm});
            skLineSegment(sketch, "E7.2.29.1", {"start": v(26.72, 35.85) * mm, "end": v(18.6, 35.85) * mm});
            skLineSegment(sketch, "E7.2.29.2", {"start": v(26.72, 35.85) * mm, "end": v(26.72, 36.35) * mm});
            skLineSegment(sketch, "E7.2.29.3", {"start": v(18.6, 35.85) * mm, "end": v(18.6, 36.35) * mm});
            skLineSegment(sketch, "E7.2.30.0", {"start": v(26.72, 37.35) * mm, "end": v(18.6, 37.35) * mm});
            skLineSegment(sketch, "E7.2.30.1", {"start": v(26.72, 36.85) * mm, "end": v(18.6, 36.85) * mm});
            skLineSegment(sketch, "E7.2.30.2", {"start": v(26.72, 36.85) * mm, "end": v(26.72, 37.35) * mm});
            skLineSegment(sketch, "E7.2.30.3", {"start": v(18.6, 36.85) * mm, "end": v(18.6, 37.35) * mm});
            skLineSegment(sketch, "E7.2.31.0", {"start": v(26.72, 38.35) * mm, "end": v(18.6, 38.35) * mm});
            skLineSegment(sketch, "E7.2.31.1", {"start": v(26.72, 37.85) * mm, "end": v(18.6, 37.85) * mm});
            skLineSegment(sketch, "E7.2.31.2", {"start": v(26.72, 37.85) * mm, "end": v(26.72, 38.35) * mm});
            skLineSegment(sketch, "E7.2.31.3", {"start": v(18.6, 37.85) * mm, "end": v(18.6, 38.35) * mm});
            skLineSegment(sketch, "E7.2.32.0", {"start": v(26.72, 39.35) * mm, "end": v(18.6, 39.35) * mm});
            skLineSegment(sketch, "E7.2.32.1", {"start": v(26.72, 38.85) * mm, "end": v(18.6, 38.85) * mm});
            skLineSegment(sketch, "E7.2.32.2", {"start": v(26.72, 38.85) * mm, "end": v(26.72, 39.35) * mm});
            skLineSegment(sketch, "E7.2.32.3", {"start": v(18.6, 38.85) * mm, "end": v(18.6, 39.35) * mm});
            skLineSegment(sketch, "E7.2.33.0", {"start": v(26.72, 40.35) * mm, "end": v(18.6, 40.35) * mm});
            skLineSegment(sketch, "E7.2.33.1", {"start": v(26.72, 39.85) * mm, "end": v(18.6, 39.85) * mm});
            skLineSegment(sketch, "E7.2.33.2", {"start": v(26.72, 39.85) * mm, "end": v(26.72, 40.35) * mm});
            skLineSegment(sketch, "E7.2.33.3", {"start": v(18.6, 39.85) * mm, "end": v(18.6, 40.35) * mm});
            skLineSegment(sketch, "E7.2.34.0", {"start": v(26.72, 41.35) * mm, "end": v(18.6, 41.35) * mm});
            skLineSegment(sketch, "E7.2.34.1", {"start": v(26.72, 40.85) * mm, "end": v(18.6, 40.85) * mm});
            skLineSegment(sketch, "E7.2.34.2", {"start": v(26.72, 40.85) * mm, "end": v(26.72, 41.35) * mm});
            skLineSegment(sketch, "E7.2.34.3", {"start": v(18.6, 40.85) * mm, "end": v(18.6, 41.35) * mm});
            skLineSegment(sketch, "E7.2.35.0", {"start": v(26.72, 42.35) * mm, "end": v(18.6, 42.35) * mm});
            skLineSegment(sketch, "E7.2.35.1", {"start": v(26.72, 41.85) * mm, "end": v(18.6, 41.85) * mm});
            skLineSegment(sketch, "E7.2.35.2", {"start": v(26.72, 41.85) * mm, "end": v(26.72, 42.35) * mm});
            skLineSegment(sketch, "E7.2.35.3", {"start": v(18.6, 41.85) * mm, "end": v(18.6, 42.35) * mm});
            skLineSegment(sketch, "E7.2.36.0", {"start": v(26.72, 43.35) * mm, "end": v(18.6, 43.35) * mm});
            skLineSegment(sketch, "E7.2.36.1", {"start": v(26.72, 42.85) * mm, "end": v(18.6, 42.85) * mm});
            skLineSegment(sketch, "E7.2.36.2", {"start": v(26.72, 42.85) * mm, "end": v(26.72, 43.35) * mm});
            skLineSegment(sketch, "E7.2.36.3", {"start": v(18.6, 42.85) * mm, "end": v(18.6, 43.35) * mm});
            skLineSegment(sketch, "E7.2.37.0", {"start": v(26.72, 44.35) * mm, "end": v(18.6, 44.35) * mm});
            skLineSegment(sketch, "E7.2.37.1", {"start": v(26.72, 43.85) * mm, "end": v(18.6, 43.85) * mm});
            skLineSegment(sketch, "E7.2.37.2", {"start": v(26.72, 43.85) * mm, "end": v(26.72, 44.35) * mm});
            skLineSegment(sketch, "E7.2.37.3", {"start": v(18.6, 43.85) * mm, "end": v(18.6, 44.35) * mm});
            skLineSegment(sketch, "E7.2.38.0", {"start": v(26.72, 45.35) * mm, "end": v(18.6, 45.35) * mm});
            skLineSegment(sketch, "E7.2.38.1", {"start": v(26.72, 44.85) * mm, "end": v(18.6, 44.85) * mm});
            skLineSegment(sketch, "E7.2.38.2", {"start": v(26.72, 44.85) * mm, "end": v(26.72, 45.35) * mm});
            skLineSegment(sketch, "E7.2.38.3", {"start": v(18.6, 44.85) * mm, "end": v(18.6, 45.35) * mm});
            skLineSegment(sketch, "E7.2.39.0", {"start": v(26.72, 46.35) * mm, "end": v(18.6, 46.35) * mm});
            skLineSegment(sketch, "E7.2.39.1", {"start": v(26.72, 45.85) * mm, "end": v(18.6, 45.85) * mm});
            skLineSegment(sketch, "E7.2.39.2", {"start": v(26.72, 45.85) * mm, "end": v(26.72, 46.35) * mm});
            skLineSegment(sketch, "E7.2.39.3", {"start": v(18.6, 45.85) * mm, "end": v(18.6, 46.35) * mm});
            skLineSegment(sketch, "E7.2.40.0", {"start": v(26.72, 47.35) * mm, "end": v(18.6, 47.35) * mm});
            skLineSegment(sketch, "E7.2.40.1", {"start": v(26.72, 46.85) * mm, "end": v(18.6, 46.85) * mm});
            skLineSegment(sketch, "E7.2.40.2", {"start": v(26.72, 46.85) * mm, "end": v(26.72, 47.35) * mm});
            skLineSegment(sketch, "E7.2.40.3", {"start": v(18.6, 46.85) * mm, "end": v(18.6, 47.35) * mm});
            skLineSegment(sketch, "E7.2.41.0", {"start": v(26.72, 48.35) * mm, "end": v(18.6, 48.35) * mm});
            skLineSegment(sketch, "E7.2.41.1", {"start": v(26.72, 47.85) * mm, "end": v(18.6, 47.85) * mm});
            skLineSegment(sketch, "E7.2.41.2", {"start": v(26.72, 47.85) * mm, "end": v(26.72, 48.35) * mm});
            skLineSegment(sketch, "E7.2.41.3", {"start": v(18.6, 47.85) * mm, "end": v(18.6, 48.35) * mm});
            skLineSegment(sketch, "E7.2.42.0", {"start": v(26.72, 49.35) * mm, "end": v(18.6, 49.35) * mm});
            skLineSegment(sketch, "E7.2.42.1", {"start": v(26.72, 48.85) * mm, "end": v(18.6, 48.85) * mm});
            skLineSegment(sketch, "E7.2.42.2", {"start": v(26.72, 48.85) * mm, "end": v(26.72, 49.35) * mm});
            skLineSegment(sketch, "E7.2.42.3", {"start": v(18.6, 48.85) * mm, "end": v(18.6, 49.35) * mm});
            skLineSegment(sketch, "E7.2.43.0", {"start": v(26.72, 50.35) * mm, "end": v(18.6, 50.35) * mm});
            skLineSegment(sketch, "E7.2.43.1", {"start": v(26.72, 49.85) * mm, "end": v(18.6, 49.85) * mm});
            skLineSegment(sketch, "E7.2.43.2", {"start": v(26.72, 49.85) * mm, "end": v(26.72, 50.35) * mm});
            skLineSegment(sketch, "E7.2.43.3", {"start": v(18.6, 49.85) * mm, "end": v(18.6, 50.35) * mm});
            skLineSegment(sketch, "E7.2.44.0", {"start": v(26.72, 51.35) * mm, "end": v(18.6, 51.35) * mm});
            skLineSegment(sketch, "E7.2.44.1", {"start": v(26.72, 50.85) * mm, "end": v(18.6, 50.85) * mm});
            skLineSegment(sketch, "E7.2.44.2", {"start": v(26.72, 50.85) * mm, "end": v(26.72, 51.35) * mm});
            skLineSegment(sketch, "E7.2.44.3", {"start": v(18.6, 50.85) * mm, "end": v(18.6, 51.35) * mm});
            skLineSegment(sketch, "E7.2.45.0", {"start": v(26.72, 52.35) * mm, "end": v(18.6, 52.35) * mm});
            skLineSegment(sketch, "E7.2.45.1", {"start": v(26.72, 51.85) * mm, "end": v(18.6, 51.85) * mm});
            skLineSegment(sketch, "E7.2.45.2", {"start": v(26.72, 51.85) * mm, "end": v(26.72, 52.35) * mm});
            skLineSegment(sketch, "E7.2.45.3", {"start": v(18.6, 51.85) * mm, "end": v(18.6, 52.35) * mm});
            skLineSegment(sketch, "E7.2.46.0", {"start": v(26.72, 53.35) * mm, "end": v(18.6, 53.35) * mm});
            skLineSegment(sketch, "E7.2.46.1", {"start": v(26.72, 52.85) * mm, "end": v(18.6, 52.85) * mm});
            skLineSegment(sketch, "E7.2.46.2", {"start": v(26.72, 52.85) * mm, "end": v(26.72, 53.35) * mm});
            skLineSegment(sketch, "E7.2.46.3", {"start": v(18.6, 52.85) * mm, "end": v(18.6, 53.35) * mm});
            skLineSegment(sketch, "E7.2.47.0", {"start": v(26.72, 54.35) * mm, "end": v(18.6, 54.35) * mm});
            skLineSegment(sketch, "E7.2.47.1", {"start": v(26.72, 53.85) * mm, "end": v(18.6, 53.85) * mm});
            skLineSegment(sketch, "E7.2.47.2", {"start": v(26.72, 53.85) * mm, "end": v(26.72, 54.35) * mm});
            skLineSegment(sketch, "E7.2.47.3", {"start": v(18.6, 53.85) * mm, "end": v(18.6, 54.35) * mm});
            skLineSegment(sketch, "E7.2.48.0", {"start": v(26.72, 55.35) * mm, "end": v(18.6, 55.35) * mm});
            skLineSegment(sketch, "E7.2.48.1", {"start": v(26.72, 54.85) * mm, "end": v(18.6, 54.85) * mm});
            skLineSegment(sketch, "E7.2.48.2", {"start": v(26.72, 54.85) * mm, "end": v(26.72, 55.35) * mm});
            skLineSegment(sketch, "E7.2.48.3", {"start": v(18.6, 54.85) * mm, "end": v(18.6, 55.35) * mm});
            skLineSegment(sketch, "E7.2.49.0", {"start": v(26.72, 56.35) * mm, "end": v(18.6, 56.35) * mm});
            skLineSegment(sketch, "E7.2.49.1", {"start": v(26.72, 55.85) * mm, "end": v(18.6, 55.85) * mm});
            skLineSegment(sketch, "E7.2.49.2", {"start": v(26.72, 55.85) * mm, "end": v(26.72, 56.35) * mm});
            skLineSegment(sketch, "E7.2.49.3", {"start": v(18.6, 55.85) * mm, "end": v(18.6, 56.35) * mm});
            skLineSegment(sketch, "E7.2.50.0", {"start": v(26.72, 57.35) * mm, "end": v(18.6, 57.35) * mm});
            skLineSegment(sketch, "E7.2.50.1", {"start": v(26.72, 56.85) * mm, "end": v(18.6, 56.85) * mm});
            skLineSegment(sketch, "E7.2.50.2", {"start": v(26.72, 56.85) * mm, "end": v(26.72, 57.35) * mm});
            skLineSegment(sketch, "E7.2.50.3", {"start": v(18.6, 56.85) * mm, "end": v(18.6, 57.35) * mm});
            skLineSegment(sketch, "E7.2.51.0", {"start": v(26.72, 58.35) * mm, "end": v(18.6, 58.35) * mm});
            skLineSegment(sketch, "E7.2.51.1", {"start": v(26.72, 57.85) * mm, "end": v(18.6, 57.85) * mm});
            skLineSegment(sketch, "E7.2.51.2", {"start": v(26.72, 57.85) * mm, "end": v(26.72, 58.35) * mm});
            skLineSegment(sketch, "E7.2.51.3", {"start": v(18.6, 57.85) * mm, "end": v(18.6, 58.35) * mm});
            skLineSegment(sketch, "E7.2.52.0", {"start": v(26.72, 59.35) * mm, "end": v(18.6, 59.35) * mm});
            skLineSegment(sketch, "E7.2.52.1", {"start": v(26.72, 58.85) * mm, "end": v(18.6, 58.85) * mm});
            skLineSegment(sketch, "E7.2.52.2", {"start": v(26.72, 58.85) * mm, "end": v(26.72, 59.35) * mm});
            skLineSegment(sketch, "E7.2.52.3", {"start": v(18.6, 58.85) * mm, "end": v(18.6, 59.35) * mm});
            skLineSegment(sketch, "E7.2.53.0", {"start": v(26.72, 60.35) * mm, "end": v(18.6, 60.35) * mm});
            skLineSegment(sketch, "E7.2.53.1", {"start": v(26.72, 59.85) * mm, "end": v(18.6, 59.85) * mm});
            skLineSegment(sketch, "E7.2.53.2", {"start": v(26.72, 59.85) * mm, "end": v(26.72, 60.35) * mm});
            skLineSegment(sketch, "E7.2.53.3", {"start": v(18.6, 59.85) * mm, "end": v(18.6, 60.35) * mm});
            skLineSegment(sketch, "E7.2.54.0", {"start": v(26.72, 61.35) * mm, "end": v(18.6, 61.35) * mm});
            skLineSegment(sketch, "E7.2.54.1", {"start": v(26.72, 60.85) * mm, "end": v(18.6, 60.85) * mm});
            skLineSegment(sketch, "E7.2.54.2", {"start": v(26.72, 60.85) * mm, "end": v(26.72, 61.35) * mm});
            skLineSegment(sketch, "E7.2.54.3", {"start": v(18.6, 60.85) * mm, "end": v(18.6, 61.35) * mm});
            skLineSegment(sketch, "E7.2.55.0", {"start": v(26.72, 62.35) * mm, "end": v(18.6, 62.35) * mm});
            skLineSegment(sketch, "E7.2.55.1", {"start": v(26.72, 61.85) * mm, "end": v(18.6, 61.85) * mm});
            skLineSegment(sketch, "E7.2.55.2", {"start": v(26.72, 61.85) * mm, "end": v(26.72, 62.35) * mm});
            skLineSegment(sketch, "E7.2.55.3", {"start": v(18.6, 61.85) * mm, "end": v(18.6, 62.35) * mm});
            skLineSegment(sketch, "E7.2.56.0", {"start": v(26.72, 63.35) * mm, "end": v(18.6, 63.35) * mm});
            skLineSegment(sketch, "E7.2.56.1", {"start": v(26.72, 62.85) * mm, "end": v(18.6, 62.85) * mm});
            skLineSegment(sketch, "E7.2.56.2", {"start": v(26.72, 62.85) * mm, "end": v(26.72, 63.35) * mm});
            skLineSegment(sketch, "E7.2.56.3", {"start": v(18.6, 62.85) * mm, "end": v(18.6, 63.35) * mm});
            skLineSegment(sketch, "E7.2.57.0", {"start": v(26.72, 64.35) * mm, "end": v(18.6, 64.35) * mm});
            skLineSegment(sketch, "E7.2.57.1", {"start": v(26.72, 63.85) * mm, "end": v(18.6, 63.85) * mm});
            skLineSegment(sketch, "E7.2.57.2", {"start": v(26.72, 63.85) * mm, "end": v(26.72, 64.35) * mm});
            skLineSegment(sketch, "E7.2.57.3", {"start": v(18.6, 63.85) * mm, "end": v(18.6, 64.35) * mm});
            skLineSegment(sketch, "E7.2.58.0", {"start": v(26.72, 65.35) * mm, "end": v(18.6, 65.35) * mm});
            skLineSegment(sketch, "E7.2.58.1", {"start": v(26.72, 64.85) * mm, "end": v(18.6, 64.85) * mm});
            skLineSegment(sketch, "E7.2.58.2", {"start": v(26.72, 64.85) * mm, "end": v(26.72, 65.35) * mm});
            skLineSegment(sketch, "E7.2.58.3", {"start": v(18.6, 64.85) * mm, "end": v(18.6, 65.35) * mm});
            skLineSegment(sketch, "E7.2.59.0", {"start": v(26.72, 66.35) * mm, "end": v(18.6, 66.35) * mm});
            skLineSegment(sketch, "E7.2.59.1", {"start": v(26.72, 65.85) * mm, "end": v(18.6, 65.85) * mm});
            skLineSegment(sketch, "E7.2.59.2", {"start": v(26.72, 65.85) * mm, "end": v(26.72, 66.35) * mm});
            skLineSegment(sketch, "E7.2.59.3", {"start": v(18.6, 65.85) * mm, "end": v(18.6, 66.35) * mm});
            skLineSegment(sketch, "E7.2.60.0", {"start": v(26.72, 67.35) * mm, "end": v(18.6, 67.35) * mm});
            skLineSegment(sketch, "E7.2.60.1", {"start": v(26.72, 66.85) * mm, "end": v(18.6, 66.85) * mm});
            skLineSegment(sketch, "E7.2.60.2", {"start": v(26.72, 66.85) * mm, "end": v(26.72, 67.35) * mm});
            skLineSegment(sketch, "E7.2.60.3", {"start": v(18.6, 66.85) * mm, "end": v(18.6, 67.35) * mm});
            skLineSegment(sketch, "E7.2.61.0", {"start": v(26.72, 68.35) * mm, "end": v(18.6, 68.35) * mm});
            skLineSegment(sketch, "E7.2.61.1", {"start": v(26.72, 67.85) * mm, "end": v(18.6, 67.85) * mm});
            skLineSegment(sketch, "E7.2.61.2", {"start": v(26.72, 67.85) * mm, "end": v(26.72, 68.35) * mm});
            skLineSegment(sketch, "E7.2.61.3", {"start": v(18.6, 67.85) * mm, "end": v(18.6, 68.35) * mm});
            skLineSegment(sketch, "E7.2.62.0", {"start": v(26.72, 69.35) * mm, "end": v(18.6, 69.35) * mm});
            skLineSegment(sketch, "E7.2.62.1", {"start": v(26.72, 68.85) * mm, "end": v(18.6, 68.85) * mm});
            skLineSegment(sketch, "E7.2.62.2", {"start": v(26.72, 68.85) * mm, "end": v(26.72, 69.35) * mm});
            skLineSegment(sketch, "E7.2.62.3", {"start": v(18.6, 68.85) * mm, "end": v(18.6, 69.35) * mm});
            skLineSegment(sketch, "E7.2.63.0", {"start": v(26.72, 70.35) * mm, "end": v(18.6, 70.35) * mm});
            skLineSegment(sketch, "E7.2.63.1", {"start": v(26.72, 69.85) * mm, "end": v(18.6, 69.85) * mm});
            skLineSegment(sketch, "E7.2.63.2", {"start": v(26.72, 69.85) * mm, "end": v(26.72, 70.35) * mm});
            skLineSegment(sketch, "E7.2.63.3", {"start": v(18.6, 69.85) * mm, "end": v(18.6, 70.35) * mm});
            skLineSegment(sketch, "E7.2.64.0", {"start": v(26.72, 71.35) * mm, "end": v(18.6, 71.35) * mm});
            skLineSegment(sketch, "E7.2.64.1", {"start": v(26.72, 70.85) * mm, "end": v(18.6, 70.85) * mm});
            skLineSegment(sketch, "E7.2.64.2", {"start": v(26.72, 70.85) * mm, "end": v(26.72, 71.35) * mm});
            skLineSegment(sketch, "E7.2.64.3", {"start": v(18.6, 70.85) * mm, "end": v(18.6, 71.35) * mm});
            skLineSegment(sketch, "E7.2.65.0", {"start": v(26.72, 72.35) * mm, "end": v(18.6, 72.35) * mm});
            skLineSegment(sketch, "E7.2.65.1", {"start": v(26.72, 71.85) * mm, "end": v(18.6, 71.85) * mm});
            skLineSegment(sketch, "E7.2.65.2", {"start": v(26.72, 71.85) * mm, "end": v(26.72, 72.35) * mm});
            skLineSegment(sketch, "E7.2.65.3", {"start": v(18.6, 71.85) * mm, "end": v(18.6, 72.35) * mm});
            skLineSegment(sketch, "E7.2.66.0", {"start": v(26.72, 73.35) * mm, "end": v(18.6, 73.35) * mm});
            skLineSegment(sketch, "E7.2.66.1", {"start": v(26.72, 72.85) * mm, "end": v(18.6, 72.85) * mm});
            skLineSegment(sketch, "E7.2.66.2", {"start": v(26.72, 72.85) * mm, "end": v(26.72, 73.35) * mm});
            skLineSegment(sketch, "E7.2.66.3", {"start": v(18.6, 72.85) * mm, "end": v(18.6, 73.35) * mm});
            skLineSegment(sketch, "E7.2.67.0", {"start": v(26.72, 74.35) * mm, "end": v(18.6, 74.35) * mm});
            skLineSegment(sketch, "E7.2.67.1", {"start": v(26.72, 73.85) * mm, "end": v(18.6, 73.85) * mm});
            skLineSegment(sketch, "E7.2.67.2", {"start": v(26.72, 73.85) * mm, "end": v(26.72, 74.35) * mm});
            skLineSegment(sketch, "E7.2.67.3", {"start": v(18.6, 73.85) * mm, "end": v(18.6, 74.35) * mm});
            skLineSegment(sketch, "E7.2.68.0", {"start": v(26.72, 75.35) * mm, "end": v(18.6, 75.35) * mm});
            skLineSegment(sketch, "E7.2.68.1", {"start": v(26.72, 74.85) * mm, "end": v(18.6, 74.85) * mm});
            skLineSegment(sketch, "E7.2.68.2", {"start": v(26.72, 74.85) * mm, "end": v(26.72, 75.35) * mm});
            skLineSegment(sketch, "E7.2.68.3", {"start": v(18.6, 74.85) * mm, "end": v(18.6, 75.35) * mm});
            skLineSegment(sketch, "E7.direction1", {"start": v(-26.72, 6.85) * mm, "end": v(-4.06, 6.85) * mm, "construction": true});
            skLineSegment(sketch, "E7.direction2", {"start": v(-26.72, 6.85) * mm, "end": v(-26.72, 7.85) * mm, "construction": true});
            skSolve(sketch);
        }
        {
            var Q0;
            Q0 = qSketchRegion(id + "F6", true);
            extrude(context, id + "F7", {"entities" : qUnion([Q0]), "depth" : 5 * mm, "offsetDistance" : 25.4 * mm});
        }
        {
            var Q0;
            Q0=makeQuery(id+"F1.opExtrude","SWEPT_FACE",FACE,{"disambiguationData":[OSD([sQuery(id+"F0.wireOp",EDGE,"E0.bottom")])]});
            var sketch = newSketch(context, id + "F8", { "sketchPlane" : qUnion([Q0])});
            skLineSegment(sketch, "E8.bottom", {"start": v(-39.07, 76.2) * mm, "end": v(-26.72, 76.2) * mm});
            skLineSegment(sketch, "E8.top", {"start": v(-39.07, 0) * mm, "end": v(39.07, 0) * mm});
            skLineSegment(sketch, "E8.left", {"start": v(-39.07, 76.2) * mm, "end": v(-39.07, 0) * mm});
            skLineSegment(sketch, "E8.right", {"start": v(39.07, 76.2) * mm, "end": v(39.07, 0) * mm});
            skLineSegment(sketch, "E9.top", {"start": v(-26.72, 6.35) * mm, "end": v(-18.6, 6.35) * mm});
            skLineSegment(sketch, "E9.left", {"start": v(-26.72, 76.2) * mm, "end": v(-26.72, 6.35) * mm});
            skLineSegment(sketch, "E9.right", {"start": v(-18.6, 76.2) * mm, "end": v(-18.6, 6.35) * mm});
            skLineSegment(sketch, "E10.top", {"start": v(-4.06, 6.35) * mm, "end": v(4.06, 6.35) * mm});
            skLineSegment(sketch, "E10.left", {"start": v(-4.06, 76.2) * mm, "end": v(-4.06, 6.35) * mm});
            skLineSegment(sketch, "E10.right", {"start": v(4.06, 76.2) * mm, "end": v(4.06, 6.35) * mm});
            skLineSegment(sketch, "E11.top", {"start": v(18.6, 6.35) * mm, "end": v(26.72, 6.35) * mm});
            skLineSegment(sketch, "E11.left", {"start": v(18.6, 76.2) * mm, "end": v(18.6, 6.35) * mm});
            skLineSegment(sketch, "E11.right", {"start": v(26.72, 76.2) * mm, "end": v(26.72, 6.35) * mm});
            skLineSegment(sketch, "E12.trimOffspring", {"start": v(4.06, 76.2) * mm, "end": v(18.6, 76.2) * mm});
            skLineSegment(sketch, "E13.trimOffspring", {"start": v(-18.6, 76.2) * mm, "end": v(-4.06, 76.2) * mm});
            skLineSegment(sketch, "E14.trimOffspring", {"start": v(26.72, 76.2) * mm, "end": v(39.07, 76.2) * mm});
            skSolve(sketch);
        }
        {
            var Q0;
            Q0 = qSketchRegion(id + "F8", true);
            extrude(context, id + "F9", {"entities" : qUnion([Q0]), "depth" : 5 * mm, "offsetDistance" : 25.4 * mm});
        }
    });
